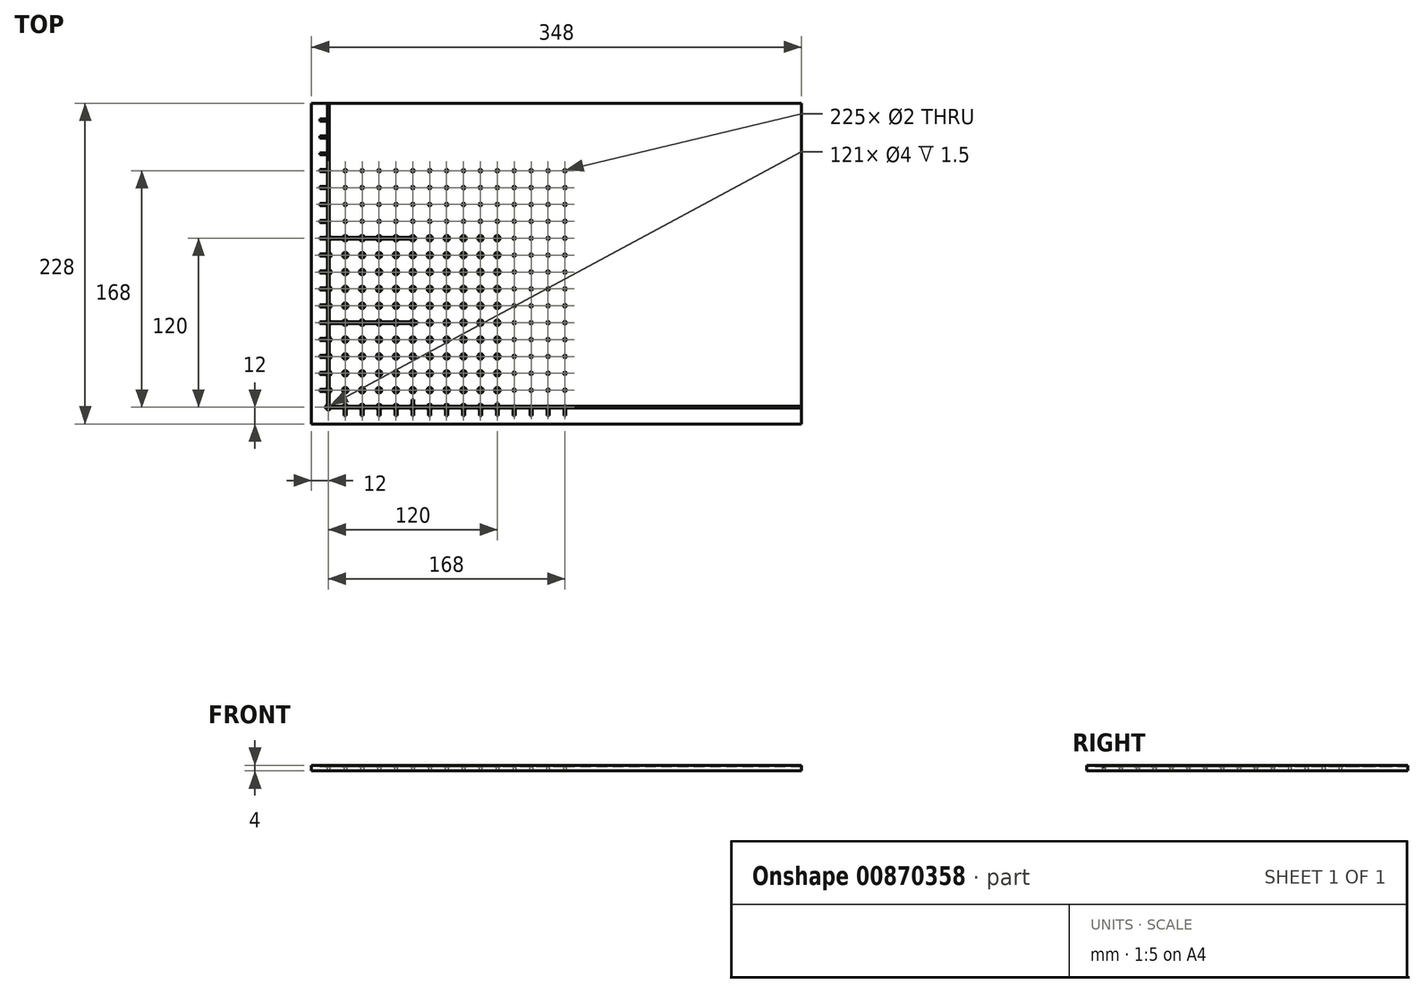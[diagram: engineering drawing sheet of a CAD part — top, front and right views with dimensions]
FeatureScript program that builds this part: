
annotation { "Feature Type Name" : "Feature", "Feature Type Description" : "" }
export const myFeature = defineFeature(function(context is Context, id is Id, definition is map)
    precondition{}
    {
        {
            var Q0;
            Q0=qCreatedBy(makeId("Top.planeOp"),FACE);
            var sketch = newSketch(context, id + "F0", { "sketchPlane" : qUnion([Q0])});
            skLineSegment(sketch, "E0.bottom", {"start": v(-174, -114) * mm, "end": v(174, -114) * mm});
            skLineSegment(sketch, "E0.top", {"start": v(-174, 114) * mm, "end": v(174, 114) * mm});
            skLineSegment(sketch, "E0.left", {"start": v(-174, -114) * mm, "end": v(-174, 114) * mm});
            skLineSegment(sketch, "E0.right", {"start": v(174, -114) * mm, "end": v(174, 114) * mm});
            skPoint(sketch, "E0.middle", {"position": v(-82, -38) * mm});
            skCircle(sketch, "E1", {"center": v(-162, 66) * mm, "radius": 1 * mm});
            skCircle(sketch, "E2.0.1.0", {"center": v(-162, 54) * mm, "radius": 1 * mm});
            skCircle(sketch, "E2.0.2.0", {"center": v(-162, 42) * mm, "radius": 1 * mm});
            skCircle(sketch, "E2.0.3.0", {"center": v(-162, 30) * mm, "radius": 1 * mm});
            skCircle(sketch, "E2.0.4.0", {"center": v(-162, 18) * mm, "radius": 1 * mm});
            skCircle(sketch, "E2.0.5.0", {"center": v(-162, 6) * mm, "radius": 1 * mm});
            skCircle(sketch, "E2.0.6.0", {"center": v(-162, -6) * mm, "radius": 1 * mm});
            skCircle(sketch, "E2.0.7.0", {"center": v(-162, -18) * mm, "radius": 1 * mm});
            skCircle(sketch, "E2.0.8.0", {"center": v(-162, -30) * mm, "radius": 1 * mm});
            skCircle(sketch, "E2.0.9.0", {"center": v(-162, -42) * mm, "radius": 1 * mm});
            skCircle(sketch, "E2.0.10.0", {"center": v(-162, -54) * mm, "radius": 1 * mm});
            skCircle(sketch, "E2.0.11.0", {"center": v(-162, -66) * mm, "radius": 1 * mm});
            skCircle(sketch, "E2.0.12.0", {"center": v(-162, -78) * mm, "radius": 1 * mm});
            skCircle(sketch, "E2.0.13.0", {"center": v(-162, -90) * mm, "radius": 1 * mm});
            skCircle(sketch, "E2.0.14.0", {"center": v(-162, -102) * mm, "radius": 1 * mm});
            skLineSegment(sketch, "E2.direction1", {"start": v(-162, 66) * mm, "end": v(-150, 66) * mm, "construction": true});
            skLineSegment(sketch, "E2.direction2", {"start": v(-162, 66) * mm, "end": v(-162, 54) * mm, "construction": true});
            skCircle(sketch, "E3.0.1.0", {"center": v(-150, 66) * mm, "radius": 1 * mm});
            skCircle(sketch, "E3.0.1.1", {"center": v(-150, 54) * mm, "radius": 1 * mm});
            skCircle(sketch, "E3.0.1.2", {"center": v(-150, 42) * mm, "radius": 1 * mm});
            skCircle(sketch, "E3.0.1.3", {"center": v(-150, 30) * mm, "radius": 1 * mm});
            skCircle(sketch, "E3.0.1.4", {"center": v(-150, 18) * mm, "radius": 1 * mm});
            skCircle(sketch, "E3.0.1.5", {"center": v(-150, 6) * mm, "radius": 1 * mm});
            skCircle(sketch, "E3.0.1.6", {"center": v(-150, -6) * mm, "radius": 1 * mm});
            skCircle(sketch, "E3.0.1.7", {"center": v(-150, -18) * mm, "radius": 1 * mm});
            skCircle(sketch, "E3.0.1.8", {"center": v(-150, -30) * mm, "radius": 1 * mm});
            skCircle(sketch, "E3.0.1.9", {"center": v(-150, -42) * mm, "radius": 1 * mm});
            skCircle(sketch, "E3.0.1.10", {"center": v(-150, -54) * mm, "radius": 1 * mm});
            skCircle(sketch, "E3.0.1.11", {"center": v(-150, -66) * mm, "radius": 1 * mm});
            skCircle(sketch, "E3.0.1.12", {"center": v(-150, -78) * mm, "radius": 1 * mm});
            skCircle(sketch, "E3.0.1.13", {"center": v(-150, -90) * mm, "radius": 1 * mm});
            skCircle(sketch, "E3.0.1.14", {"center": v(-150, -102) * mm, "radius": 1 * mm});
            skCircle(sketch, "E3.0.2.0", {"center": v(-138, 66) * mm, "radius": 1 * mm});
            skCircle(sketch, "E3.0.2.1", {"center": v(-138, 54) * mm, "radius": 1 * mm});
            skCircle(sketch, "E3.0.2.2", {"center": v(-138, 42) * mm, "radius": 1 * mm});
            skCircle(sketch, "E3.0.2.3", {"center": v(-138, 30) * mm, "radius": 1 * mm});
            skCircle(sketch, "E3.0.2.4", {"center": v(-138, 18) * mm, "radius": 1 * mm});
            skCircle(sketch, "E3.0.2.5", {"center": v(-138, 6) * mm, "radius": 1 * mm});
            skCircle(sketch, "E3.0.2.6", {"center": v(-138, -6) * mm, "radius": 1 * mm});
            skCircle(sketch, "E3.0.2.7", {"center": v(-138, -18) * mm, "radius": 1 * mm});
            skCircle(sketch, "E3.0.2.8", {"center": v(-138, -30) * mm, "radius": 1 * mm});
            skCircle(sketch, "E3.0.2.9", {"center": v(-138, -42) * mm, "radius": 1 * mm});
            skCircle(sketch, "E3.0.2.10", {"center": v(-138, -54) * mm, "radius": 1 * mm});
            skCircle(sketch, "E3.0.2.11", {"center": v(-138, -66) * mm, "radius": 1 * mm});
            skCircle(sketch, "E3.0.2.12", {"center": v(-138, -78) * mm, "radius": 1 * mm});
            skCircle(sketch, "E3.0.2.13", {"center": v(-138, -90) * mm, "radius": 1 * mm});
            skCircle(sketch, "E3.0.2.14", {"center": v(-138, -102) * mm, "radius": 1 * mm});
            skCircle(sketch, "E3.0.3.0", {"center": v(-126, 66) * mm, "radius": 1 * mm});
            skCircle(sketch, "E3.0.3.1", {"center": v(-126, 54) * mm, "radius": 1 * mm});
            skCircle(sketch, "E3.0.3.2", {"center": v(-126, 42) * mm, "radius": 1 * mm});
            skCircle(sketch, "E3.0.3.3", {"center": v(-126, 30) * mm, "radius": 1 * mm});
            skCircle(sketch, "E3.0.3.4", {"center": v(-126, 18) * mm, "radius": 1 * mm});
            skCircle(sketch, "E3.0.3.5", {"center": v(-126, 6) * mm, "radius": 1 * mm});
            skCircle(sketch, "E3.0.3.6", {"center": v(-126, -6) * mm, "radius": 1 * mm});
            skCircle(sketch, "E3.0.3.7", {"center": v(-126, -18) * mm, "radius": 1 * mm});
            skCircle(sketch, "E3.0.3.8", {"center": v(-126, -30) * mm, "radius": 1 * mm});
            skCircle(sketch, "E3.0.3.9", {"center": v(-126, -42) * mm, "radius": 1 * mm});
            skCircle(sketch, "E3.0.3.10", {"center": v(-126, -54) * mm, "radius": 1 * mm});
            skCircle(sketch, "E3.0.3.11", {"center": v(-126, -66) * mm, "radius": 1 * mm});
            skCircle(sketch, "E3.0.3.12", {"center": v(-126, -78) * mm, "radius": 1 * mm});
            skCircle(sketch, "E3.0.3.13", {"center": v(-126, -90) * mm, "radius": 1 * mm});
            skCircle(sketch, "E3.0.3.14", {"center": v(-126, -102) * mm, "radius": 1 * mm});
            skCircle(sketch, "E3.0.4.0", {"center": v(-114, 66) * mm, "radius": 1 * mm});
            skCircle(sketch, "E3.0.4.1", {"center": v(-114, 54) * mm, "radius": 1 * mm});
            skCircle(sketch, "E3.0.4.2", {"center": v(-114, 42) * mm, "radius": 1 * mm});
            skCircle(sketch, "E3.0.4.3", {"center": v(-114, 30) * mm, "radius": 1 * mm});
            skCircle(sketch, "E3.0.4.4", {"center": v(-114, 18) * mm, "radius": 1 * mm});
            skCircle(sketch, "E3.0.4.5", {"center": v(-114, 6) * mm, "radius": 1 * mm});
            skCircle(sketch, "E3.0.4.6", {"center": v(-114, -6) * mm, "radius": 1 * mm});
            skCircle(sketch, "E3.0.4.7", {"center": v(-114, -18) * mm, "radius": 1 * mm});
            skCircle(sketch, "E3.0.4.8", {"center": v(-114, -30) * mm, "radius": 1 * mm});
            skCircle(sketch, "E3.0.4.9", {"center": v(-114, -42) * mm, "radius": 1 * mm});
            skCircle(sketch, "E3.0.4.10", {"center": v(-114, -54) * mm, "radius": 1 * mm});
            skCircle(sketch, "E3.0.4.11", {"center": v(-114, -66) * mm, "radius": 1 * mm});
            skCircle(sketch, "E3.0.4.12", {"center": v(-114, -78) * mm, "radius": 1 * mm});
            skCircle(sketch, "E3.0.4.13", {"center": v(-114, -90) * mm, "radius": 1 * mm});
            skCircle(sketch, "E3.0.4.14", {"center": v(-114, -102) * mm, "radius": 1 * mm});
            skCircle(sketch, "E3.0.5.0", {"center": v(-102, 66) * mm, "radius": 1 * mm});
            skCircle(sketch, "E3.0.5.1", {"center": v(-102, 54) * mm, "radius": 1 * mm});
            skCircle(sketch, "E3.0.5.2", {"center": v(-102, 42) * mm, "radius": 1 * mm});
            skCircle(sketch, "E3.0.5.3", {"center": v(-102, 30) * mm, "radius": 1 * mm});
            skCircle(sketch, "E3.0.5.4", {"center": v(-102, 18) * mm, "radius": 1 * mm});
            skCircle(sketch, "E3.0.5.5", {"center": v(-102, 6) * mm, "radius": 1 * mm});
            skCircle(sketch, "E3.0.5.6", {"center": v(-102, -6) * mm, "radius": 1 * mm});
            skCircle(sketch, "E3.0.5.7", {"center": v(-102, -18) * mm, "radius": 1 * mm});
            skCircle(sketch, "E3.0.5.8", {"center": v(-102, -30) * mm, "radius": 1 * mm});
            skCircle(sketch, "E3.0.5.9", {"center": v(-102, -42) * mm, "radius": 1 * mm});
            skCircle(sketch, "E3.0.5.10", {"center": v(-102, -54) * mm, "radius": 1 * mm});
            skCircle(sketch, "E3.0.5.11", {"center": v(-102, -66) * mm, "radius": 1 * mm});
            skCircle(sketch, "E3.0.5.12", {"center": v(-102, -78) * mm, "radius": 1 * mm});
            skCircle(sketch, "E3.0.5.13", {"center": v(-102, -90) * mm, "radius": 1 * mm});
            skCircle(sketch, "E3.0.5.14", {"center": v(-102, -102) * mm, "radius": 1 * mm});
            skCircle(sketch, "E3.0.6.0", {"center": v(-90, 66) * mm, "radius": 1 * mm});
            skCircle(sketch, "E3.0.6.1", {"center": v(-90, 54) * mm, "radius": 1 * mm});
            skCircle(sketch, "E3.0.6.2", {"center": v(-90, 42) * mm, "radius": 1 * mm});
            skCircle(sketch, "E3.0.6.3", {"center": v(-90, 30) * mm, "radius": 1 * mm});
            skCircle(sketch, "E3.0.6.4", {"center": v(-90, 18) * mm, "radius": 1 * mm});
            skCircle(sketch, "E3.0.6.5", {"center": v(-90, 6) * mm, "radius": 1 * mm});
            skCircle(sketch, "E3.0.6.6", {"center": v(-90, -6) * mm, "radius": 1 * mm});
            skCircle(sketch, "E3.0.6.7", {"center": v(-90, -18) * mm, "radius": 1 * mm});
            skCircle(sketch, "E3.0.6.8", {"center": v(-90, -30) * mm, "radius": 1 * mm});
            skCircle(sketch, "E3.0.6.9", {"center": v(-90, -42) * mm, "radius": 1 * mm});
            skCircle(sketch, "E3.0.6.10", {"center": v(-90, -54) * mm, "radius": 1 * mm});
            skCircle(sketch, "E3.0.6.11", {"center": v(-90, -66) * mm, "radius": 1 * mm});
            skCircle(sketch, "E3.0.6.12", {"center": v(-90, -78) * mm, "radius": 1 * mm});
            skCircle(sketch, "E3.0.6.13", {"center": v(-90, -90) * mm, "radius": 1 * mm});
            skCircle(sketch, "E3.0.6.14", {"center": v(-90, -102) * mm, "radius": 1 * mm});
            skCircle(sketch, "E3.0.7.0", {"center": v(-78, 66) * mm, "radius": 1 * mm});
            skCircle(sketch, "E3.0.7.1", {"center": v(-78, 54) * mm, "radius": 1 * mm});
            skCircle(sketch, "E3.0.7.2", {"center": v(-78, 42) * mm, "radius": 1 * mm});
            skCircle(sketch, "E3.0.7.3", {"center": v(-78, 30) * mm, "radius": 1 * mm});
            skCircle(sketch, "E3.0.7.4", {"center": v(-78, 18) * mm, "radius": 1 * mm});
            skCircle(sketch, "E3.0.7.5", {"center": v(-78, 6) * mm, "radius": 1 * mm});
            skCircle(sketch, "E3.0.7.6", {"center": v(-78, -6) * mm, "radius": 1 * mm});
            skCircle(sketch, "E3.0.7.7", {"center": v(-78, -18) * mm, "radius": 1 * mm});
            skCircle(sketch, "E3.0.7.8", {"center": v(-78, -30) * mm, "radius": 1 * mm});
            skCircle(sketch, "E3.0.7.9", {"center": v(-78, -42) * mm, "radius": 1 * mm});
            skCircle(sketch, "E3.0.7.10", {"center": v(-78, -54) * mm, "radius": 1 * mm});
            skCircle(sketch, "E3.0.7.11", {"center": v(-78, -66) * mm, "radius": 1 * mm});
            skCircle(sketch, "E3.0.7.12", {"center": v(-78, -78) * mm, "radius": 1 * mm});
            skCircle(sketch, "E3.0.7.13", {"center": v(-78, -90) * mm, "radius": 1 * mm});
            skCircle(sketch, "E3.0.7.14", {"center": v(-78, -102) * mm, "radius": 1 * mm});
            skCircle(sketch, "E3.0.8.0", {"center": v(-66, 66) * mm, "radius": 1 * mm});
            skCircle(sketch, "E3.0.8.1", {"center": v(-66, 54) * mm, "radius": 1 * mm});
            skCircle(sketch, "E3.0.8.2", {"center": v(-66, 42) * mm, "radius": 1 * mm});
            skCircle(sketch, "E3.0.8.3", {"center": v(-66, 30) * mm, "radius": 1 * mm});
            skCircle(sketch, "E3.0.8.4", {"center": v(-66, 18) * mm, "radius": 1 * mm});
            skCircle(sketch, "E3.0.8.5", {"center": v(-66, 6) * mm, "radius": 1 * mm});
            skCircle(sketch, "E3.0.8.6", {"center": v(-66, -6) * mm, "radius": 1 * mm});
            skCircle(sketch, "E3.0.8.7", {"center": v(-66, -18) * mm, "radius": 1 * mm});
            skCircle(sketch, "E3.0.8.8", {"center": v(-66, -30) * mm, "radius": 1 * mm});
            skCircle(sketch, "E3.0.8.9", {"center": v(-66, -42) * mm, "radius": 1 * mm});
            skCircle(sketch, "E3.0.8.10", {"center": v(-66, -54) * mm, "radius": 1 * mm});
            skCircle(sketch, "E3.0.8.11", {"center": v(-66, -66) * mm, "radius": 1 * mm});
            skCircle(sketch, "E3.0.8.12", {"center": v(-66, -78) * mm, "radius": 1 * mm});
            skCircle(sketch, "E3.0.8.13", {"center": v(-66, -90) * mm, "radius": 1 * mm});
            skCircle(sketch, "E3.0.8.14", {"center": v(-66, -102) * mm, "radius": 1 * mm});
            skCircle(sketch, "E3.0.9.0", {"center": v(-54, 66) * mm, "radius": 1 * mm});
            skCircle(sketch, "E3.0.9.1", {"center": v(-54, 54) * mm, "radius": 1 * mm});
            skCircle(sketch, "E3.0.9.2", {"center": v(-54, 42) * mm, "radius": 1 * mm});
            skCircle(sketch, "E3.0.9.3", {"center": v(-54, 30) * mm, "radius": 1 * mm});
            skCircle(sketch, "E3.0.9.4", {"center": v(-54, 18) * mm, "radius": 1 * mm});
            skCircle(sketch, "E3.0.9.5", {"center": v(-54, 6) * mm, "radius": 1 * mm});
            skCircle(sketch, "E3.0.9.6", {"center": v(-54, -6) * mm, "radius": 1 * mm});
            skCircle(sketch, "E3.0.9.7", {"center": v(-54, -18) * mm, "radius": 1 * mm});
            skCircle(sketch, "E3.0.9.8", {"center": v(-54, -30) * mm, "radius": 1 * mm});
            skCircle(sketch, "E3.0.9.9", {"center": v(-54, -42) * mm, "radius": 1 * mm});
            skCircle(sketch, "E3.0.9.10", {"center": v(-54, -54) * mm, "radius": 1 * mm});
            skCircle(sketch, "E3.0.9.11", {"center": v(-54, -66) * mm, "radius": 1 * mm});
            skCircle(sketch, "E3.0.9.12", {"center": v(-54, -78) * mm, "radius": 1 * mm});
            skCircle(sketch, "E3.0.9.13", {"center": v(-54, -90) * mm, "radius": 1 * mm});
            skCircle(sketch, "E3.0.9.14", {"center": v(-54, -102) * mm, "radius": 1 * mm});
            skCircle(sketch, "E3.0.10.0", {"center": v(-42, 66) * mm, "radius": 1 * mm});
            skCircle(sketch, "E3.0.10.1", {"center": v(-42, 54) * mm, "radius": 1 * mm});
            skCircle(sketch, "E3.0.10.2", {"center": v(-42, 42) * mm, "radius": 1 * mm});
            skCircle(sketch, "E3.0.10.3", {"center": v(-42, 30) * mm, "radius": 1 * mm});
            skCircle(sketch, "E3.0.10.4", {"center": v(-42, 18) * mm, "radius": 1 * mm});
            skCircle(sketch, "E3.0.10.5", {"center": v(-42, 6) * mm, "radius": 1 * mm});
            skCircle(sketch, "E3.0.10.6", {"center": v(-42, -6) * mm, "radius": 1 * mm});
            skCircle(sketch, "E3.0.10.7", {"center": v(-42, -18) * mm, "radius": 1 * mm});
            skCircle(sketch, "E3.0.10.8", {"center": v(-42, -30) * mm, "radius": 1 * mm});
            skCircle(sketch, "E3.0.10.9", {"center": v(-42, -42) * mm, "radius": 1 * mm});
            skCircle(sketch, "E3.0.10.10", {"center": v(-42, -54) * mm, "radius": 1 * mm});
            skCircle(sketch, "E3.0.10.11", {"center": v(-42, -66) * mm, "radius": 1 * mm});
            skCircle(sketch, "E3.0.10.12", {"center": v(-42, -78) * mm, "radius": 1 * mm});
            skCircle(sketch, "E3.0.10.13", {"center": v(-42, -90) * mm, "radius": 1 * mm});
            skCircle(sketch, "E3.0.10.14", {"center": v(-42, -102) * mm, "radius": 1 * mm});
            skCircle(sketch, "E3.0.11.0", {"center": v(-30, 66) * mm, "radius": 1 * mm});
            skCircle(sketch, "E3.0.11.1", {"center": v(-30, 54) * mm, "radius": 1 * mm});
            skCircle(sketch, "E3.0.11.2", {"center": v(-30, 42) * mm, "radius": 1 * mm});
            skCircle(sketch, "E3.0.11.3", {"center": v(-30, 30) * mm, "radius": 1 * mm});
            skCircle(sketch, "E3.0.11.4", {"center": v(-30, 18) * mm, "radius": 1 * mm});
            skCircle(sketch, "E3.0.11.5", {"center": v(-30, 6) * mm, "radius": 1 * mm});
            skCircle(sketch, "E3.0.11.6", {"center": v(-30, -6) * mm, "radius": 1 * mm});
            skCircle(sketch, "E3.0.11.7", {"center": v(-30, -18) * mm, "radius": 1 * mm});
            skCircle(sketch, "E3.0.11.8", {"center": v(-30, -30) * mm, "radius": 1 * mm});
            skCircle(sketch, "E3.0.11.9", {"center": v(-30, -42) * mm, "radius": 1 * mm});
            skCircle(sketch, "E3.0.11.10", {"center": v(-30, -54) * mm, "radius": 1 * mm});
            skCircle(sketch, "E3.0.11.11", {"center": v(-30, -66) * mm, "radius": 1 * mm});
            skCircle(sketch, "E3.0.11.12", {"center": v(-30, -78) * mm, "radius": 1 * mm});
            skCircle(sketch, "E3.0.11.13", {"center": v(-30, -90) * mm, "radius": 1 * mm});
            skCircle(sketch, "E3.0.11.14", {"center": v(-30, -102) * mm, "radius": 1 * mm});
            skCircle(sketch, "E3.0.12.0", {"center": v(-18, 66) * mm, "radius": 1 * mm});
            skCircle(sketch, "E3.0.12.1", {"center": v(-18, 54) * mm, "radius": 1 * mm});
            skCircle(sketch, "E3.0.12.2", {"center": v(-18, 42) * mm, "radius": 1 * mm});
            skCircle(sketch, "E3.0.12.3", {"center": v(-18, 30) * mm, "radius": 1 * mm});
            skCircle(sketch, "E3.0.12.4", {"center": v(-18, 18) * mm, "radius": 1 * mm});
            skCircle(sketch, "E3.0.12.5", {"center": v(-18, 6) * mm, "radius": 1 * mm});
            skCircle(sketch, "E3.0.12.6", {"center": v(-18, -6) * mm, "radius": 1 * mm});
            skCircle(sketch, "E3.0.12.7", {"center": v(-18, -18) * mm, "radius": 1 * mm});
            skCircle(sketch, "E3.0.12.8", {"center": v(-18, -30) * mm, "radius": 1 * mm});
            skCircle(sketch, "E3.0.12.9", {"center": v(-18, -42) * mm, "radius": 1 * mm});
            skCircle(sketch, "E3.0.12.10", {"center": v(-18, -54) * mm, "radius": 1 * mm});
            skCircle(sketch, "E3.0.12.11", {"center": v(-18, -66) * mm, "radius": 1 * mm});
            skCircle(sketch, "E3.0.12.12", {"center": v(-18, -78) * mm, "radius": 1 * mm});
            skCircle(sketch, "E3.0.12.13", {"center": v(-18, -90) * mm, "radius": 1 * mm});
            skCircle(sketch, "E3.0.12.14", {"center": v(-18, -102) * mm, "radius": 1 * mm});
            skCircle(sketch, "E3.0.13.0", {"center": v(-6, 66) * mm, "radius": 1 * mm});
            skCircle(sketch, "E3.0.13.1", {"center": v(-6, 54) * mm, "radius": 1 * mm});
            skCircle(sketch, "E3.0.13.2", {"center": v(-6, 42) * mm, "radius": 1 * mm});
            skCircle(sketch, "E3.0.13.3", {"center": v(-6, 30) * mm, "radius": 1 * mm});
            skCircle(sketch, "E3.0.13.4", {"center": v(-6, 18) * mm, "radius": 1 * mm});
            skCircle(sketch, "E3.0.13.5", {"center": v(-6, 6) * mm, "radius": 1 * mm});
            skCircle(sketch, "E3.0.13.6", {"center": v(-6, -6) * mm, "radius": 1 * mm});
            skCircle(sketch, "E3.0.13.7", {"center": v(-6, -18) * mm, "radius": 1 * mm});
            skCircle(sketch, "E3.0.13.8", {"center": v(-6, -30) * mm, "radius": 1 * mm});
            skCircle(sketch, "E3.0.13.9", {"center": v(-6, -42) * mm, "radius": 1 * mm});
            skCircle(sketch, "E3.0.13.10", {"center": v(-6, -54) * mm, "radius": 1 * mm});
            skCircle(sketch, "E3.0.13.11", {"center": v(-6, -66) * mm, "radius": 1 * mm});
            skCircle(sketch, "E3.0.13.12", {"center": v(-6, -78) * mm, "radius": 1 * mm});
            skCircle(sketch, "E3.0.13.13", {"center": v(-6, -90) * mm, "radius": 1 * mm});
            skCircle(sketch, "E3.0.13.14", {"center": v(-6, -102) * mm, "radius": 1 * mm});
            skCircle(sketch, "E3.0.14.0", {"center": v(6, 66) * mm, "radius": 1 * mm});
            skCircle(sketch, "E3.0.14.1", {"center": v(6, 54) * mm, "radius": 1 * mm});
            skCircle(sketch, "E3.0.14.2", {"center": v(6, 42) * mm, "radius": 1 * mm});
            skCircle(sketch, "E3.0.14.3", {"center": v(6, 30) * mm, "radius": 1 * mm});
            skCircle(sketch, "E3.0.14.4", {"center": v(6, 18) * mm, "radius": 1 * mm});
            skCircle(sketch, "E3.0.14.5", {"center": v(6, 6) * mm, "radius": 1 * mm});
            skCircle(sketch, "E3.0.14.6", {"center": v(6, -6) * mm, "radius": 1 * mm});
            skCircle(sketch, "E3.0.14.7", {"center": v(6, -18) * mm, "radius": 1 * mm});
            skCircle(sketch, "E3.0.14.8", {"center": v(6, -30) * mm, "radius": 1 * mm});
            skCircle(sketch, "E3.0.14.9", {"center": v(6, -42) * mm, "radius": 1 * mm});
            skCircle(sketch, "E3.0.14.10", {"center": v(6, -54) * mm, "radius": 1 * mm});
            skCircle(sketch, "E3.0.14.11", {"center": v(6, -66) * mm, "radius": 1 * mm});
            skCircle(sketch, "E3.0.14.12", {"center": v(6, -78) * mm, "radius": 1 * mm});
            skCircle(sketch, "E3.0.14.13", {"center": v(6, -90) * mm, "radius": 1 * mm});
            skCircle(sketch, "E3.0.14.14", {"center": v(6, -102) * mm, "radius": 1 * mm});
            skLineSegment(sketch, "E4", {"start": v(-187.06, -102) * mm, "end": v(211.47, -102) * mm, "construction": true});
            skLineSegment(sketch, "E5", {"start": v(-162, 132.06) * mm, "end": v(-162, -148.74) * mm, "construction": true});
            skSolve(sketch);
        }
        {
            var Q0;
            Q0=qSketchRegion(id+"F0",true);
            extrude(context, id + "F1", {"entities" : qUnion([Q0]), "offsetDistance" : 25 * mm, "depth" : 4 * mm});
        }
        {
            var Q0;
            Q0=makeQuery(id+"F1.opExtrude","CAP_FACE",FACE,{"disambiguationData":[OSD([sQuery(id+"F0.wireOp",EDGE,"E0.bottom"),sQuery(id+"F0.wireOp",EDGE,"E0.top"),sQuery(id+"F0.wireOp",EDGE,"E0.left"),sQuery(id+"F0.wireOp",EDGE,"E0.right"),sQuery(id+"F0.wireOp",EDGE,"E1"),sQuery(id+"F0.wireOp",EDGE,"E2.0.1.0"),sQuery(id+"F0.wireOp",EDGE,"E2.0.2.0"),sQuery(id+"F0.wireOp",EDGE,"E2.0.3.0"),sQuery(id+"F0.wireOp",EDGE,"E2.0.4.0"),sQuery(id+"F0.wireOp",EDGE,"E2.0.5.0"),sQuery(id+"F0.wireOp",EDGE,"E2.0.6.0"),sQuery(id+"F0.wireOp",EDGE,"E2.0.7.0"),sQuery(id+"F0.wireOp",EDGE,"E2.0.8.0"),sQuery(id+"F0.wireOp",EDGE,"E2.0.9.0"),sQuery(id+"F0.wireOp",EDGE,"E2.0.10.0"),sQuery(id+"F0.wireOp",EDGE,"E2.0.11.0"),sQuery(id+"F0.wireOp",EDGE,"E2.0.12.0"),sQuery(id+"F0.wireOp",EDGE,"E2.0.13.0"),sQuery(id+"F0.wireOp",EDGE,"E2.0.14.0"),sQuery(id+"F0.wireOp",EDGE,"E2.0.15.0"),sQuery(id+"F0.wireOp",EDGE,"E2.1.0.0"),sQuery(id+"F0.wireOp",EDGE,"E2.1.1.0"),sQuery(id+"F0.wireOp",EDGE,"E2.1.2.0"),sQuery(id+"F0.wireOp",EDGE,"E2.1.3.0"),sQuery(id+"F0.wireOp",EDGE,"E2.1.4.0"),sQuery(id+"F0.wireOp",EDGE,"E2.1.5.0"),sQuery(id+"F0.wireOp",EDGE,"E2.1.6.0"),sQuery(id+"F0.wireOp",EDGE,"E2.1.7.0"),sQuery(id+"F0.wireOp",EDGE,"E2.1.8.0"),sQuery(id+"F0.wireOp",EDGE,"E2.1.9.0"),sQuery(id+"F0.wireOp",EDGE,"E2.1.10.0"),sQuery(id+"F0.wireOp",EDGE,"E2.1.11.0"),sQuery(id+"F0.wireOp",EDGE,"E2.1.12.0"),sQuery(id+"F0.wireOp",EDGE,"E2.1.13.0"),sQuery(id+"F0.wireOp",EDGE,"E2.1.14.0"),sQuery(id+"F0.wireOp",EDGE,"E2.1.15.0"),sQuery(id+"F0.wireOp",EDGE,"E2.2.0.0"),sQuery(id+"F0.wireOp",EDGE,"E2.2.1.0"),sQuery(id+"F0.wireOp",EDGE,"E2.2.2.0"),sQuery(id+"F0.wireOp",EDGE,"E2.2.3.0"),sQuery(id+"F0.wireOp",EDGE,"E2.2.4.0"),sQuery(id+"F0.wireOp",EDGE,"E2.2.5.0"),sQuery(id+"F0.wireOp",EDGE,"E2.2.6.0"),sQuery(id+"F0.wireOp",EDGE,"E2.2.7.0"),sQuery(id+"F0.wireOp",EDGE,"E2.2.8.0"),sQuery(id+"F0.wireOp",EDGE,"E2.2.9.0"),sQuery(id+"F0.wireOp",EDGE,"E2.2.10.0"),sQuery(id+"F0.wireOp",EDGE,"E2.2.11.0"),sQuery(id+"F0.wireOp",EDGE,"E2.2.12.0"),sQuery(id+"F0.wireOp",EDGE,"E2.2.13.0"),sQuery(id+"F0.wireOp",EDGE,"E2.2.14.0"),sQuery(id+"F0.wireOp",EDGE,"E2.2.15.0"),sQuery(id+"F0.wireOp",EDGE,"E2.3.0.0"),sQuery(id+"F0.wireOp",EDGE,"E2.3.1.0"),sQuery(id+"F0.wireOp",EDGE,"E2.3.11.0"),sQuery(id+"F0.wireOp",EDGE,"E2.3.12.0"),sQuery(id+"F0.wireOp",EDGE,"E2.3.13.0"),sQuery(id+"F0.wireOp",EDGE,"E2.3.14.0"),sQuery(id+"F0.wireOp",EDGE,"E2.3.15.0"),sQuery(id+"F0.wireOp",EDGE,"E2.4.0.0"),sQuery(id+"F0.wireOp",EDGE,"E2.4.1.0"),sQuery(id+"F0.wireOp",EDGE,"E2.4.2.0"),sQuery(id+"F0.wireOp",EDGE,"E2.4.11.0"),sQuery(id+"F0.wireOp",EDGE,"E2.4.12.0"),sQuery(id+"F0.wireOp",EDGE,"E2.4.13.0"),sQuery(id+"F0.wireOp",EDGE,"E2.4.14.0"),sQuery(id+"F0.wireOp",EDGE,"E2.4.15.0"),sQuery(id+"F0.wireOp",EDGE,"E2.5.0.0"),sQuery(id+"F0.wireOp",EDGE,"E2.5.1.0"),sQuery(id+"F0.wireOp",EDGE,"E2.5.11.0"),sQuery(id+"F0.wireOp",EDGE,"E2.5.12.0"),sQuery(id+"F0.wireOp",EDGE,"E2.5.13.0"),sQuery(id+"F0.wireOp",EDGE,"E2.5.14.0"),sQuery(id+"F0.wireOp",EDGE,"E2.5.15.0"),sQuery(id+"F0.wireOp",EDGE,"E2.6.0.0"),sQuery(id+"F0.wireOp",EDGE,"E2.6.1.0"),sQuery(id+"F0.wireOp",EDGE,"E2.6.2.0"),sQuery(id+"F0.wireOp",EDGE,"E2.6.11.0"),sQuery(id+"F0.wireOp",EDGE,"E2.6.12.0"),sQuery(id+"F0.wireOp",EDGE,"E2.6.13.0"),sQuery(id+"F0.wireOp",EDGE,"E2.6.14.0"),sQuery(id+"F0.wireOp",EDGE,"E2.6.15.0"),sQuery(id+"F0.wireOp",EDGE,"E2.7.0.0"),sQuery(id+"F0.wireOp",EDGE,"E2.7.1.0"),sQuery(id+"F0.wireOp",EDGE,"E2.7.2.0"),sQuery(id+"F0.wireOp",EDGE,"E2.7.3.0"),sQuery(id+"F0.wireOp",EDGE,"E2.7.4.0"),sQuery(id+"F0.wireOp",EDGE,"E2.7.5.0"),sQuery(id+"F0.wireOp",EDGE,"E2.7.6.0"),sQuery(id+"F0.wireOp",EDGE,"E2.7.7.0"),sQuery(id+"F0.wireOp",EDGE,"E2.7.8.0"),sQuery(id+"F0.wireOp",EDGE,"E2.7.9.0"),sQuery(id+"F0.wireOp",EDGE,"E2.7.10.0"),sQuery(id+"F0.wireOp",EDGE,"E2.7.11.0"),sQuery(id+"F0.wireOp",EDGE,"E2.7.12.0"),sQuery(id+"F0.wireOp",EDGE,"E2.7.13.0"),sQuery(id+"F0.wireOp",EDGE,"E2.7.14.0"),sQuery(id+"F0.wireOp",EDGE,"E2.7.15.0"),sQuery(id+"F0.wireOp",EDGE,"E2.8.0.0"),sQuery(id+"F0.wireOp",EDGE,"E2.8.1.0"),sQuery(id+"F0.wireOp",EDGE,"E2.8.2.0"),sQuery(id+"F0.wireOp",EDGE,"E2.8.3.0"),sQuery(id+"F0.wireOp",EDGE,"E2.8.4.0"),sQuery(id+"F0.wireOp",EDGE,"E2.8.5.0"),sQuery(id+"F0.wireOp",EDGE,"E2.8.6.0"),sQuery(id+"F0.wireOp",EDGE,"E2.8.7.0"),sQuery(id+"F0.wireOp",EDGE,"E2.8.8.0"),sQuery(id+"F0.wireOp",EDGE,"E2.8.9.0"),sQuery(id+"F0.wireOp",EDGE,"E2.8.10.0"),sQuery(id+"F0.wireOp",EDGE,"E2.8.11.0"),sQuery(id+"F0.wireOp",EDGE,"E2.8.12.0"),sQuery(id+"F0.wireOp",EDGE,"E2.8.13.0"),sQuery(id+"F0.wireOp",EDGE,"E2.8.14.0"),sQuery(id+"F0.wireOp",EDGE,"E2.8.15.0"),sQuery(id+"F0.wireOp",EDGE,"E2.9.0.0"),sQuery(id+"F0.wireOp",EDGE,"E2.9.1.0"),sQuery(id+"F0.wireOp",EDGE,"E2.9.2.0"),sQuery(id+"F0.wireOp",EDGE,"E2.9.3.0"),sQuery(id+"F0.wireOp",EDGE,"E2.9.4.0"),sQuery(id+"F0.wireOp",EDGE,"E2.9.5.0"),sQuery(id+"F0.wireOp",EDGE,"E2.9.6.0"),sQuery(id+"F0.wireOp",EDGE,"E2.9.7.0"),sQuery(id+"F0.wireOp",EDGE,"E2.9.8.0"),sQuery(id+"F0.wireOp",EDGE,"E2.9.9.0"),sQuery(id+"F0.wireOp",EDGE,"E2.9.10.0"),sQuery(id+"F0.wireOp",EDGE,"E2.9.11.0"),sQuery(id+"F0.wireOp",EDGE,"E2.9.12.0"),sQuery(id+"F0.wireOp",EDGE,"E2.9.13.0"),sQuery(id+"F0.wireOp",EDGE,"E2.9.14.0"),sQuery(id+"F0.wireOp",EDGE,"E2.9.15.0"),sQuery(id+"F0.wireOp",EDGE,"E2.10.0.0"),sQuery(id+"F0.wireOp",EDGE,"E2.10.1.0"),sQuery(id+"F0.wireOp",EDGE,"E2.10.2.0"),sQuery(id+"F0.wireOp",EDGE,"E2.10.3.0"),sQuery(id+"F0.wireOp",EDGE,"E2.10.4.0"),sQuery(id+"F0.wireOp",EDGE,"E2.10.5.0"),sQuery(id+"F0.wireOp",EDGE,"E2.10.6.0"),sQuery(id+"F0.wireOp",EDGE,"E2.10.7.0"),sQuery(id+"F0.wireOp",EDGE,"E2.10.8.0"),sQuery(id+"F0.wireOp",EDGE,"E2.10.9.0"),sQuery(id+"F0.wireOp",EDGE,"E2.10.10.0"),sQuery(id+"F0.wireOp",EDGE,"E2.10.11.0"),sQuery(id+"F0.wireOp",EDGE,"E2.10.12.0"),sQuery(id+"F0.wireOp",EDGE,"E2.10.13.0"),sQuery(id+"F0.wireOp",EDGE,"E2.10.14.0"),sQuery(id+"F0.wireOp",EDGE,"E2.10.15.0"),sQuery(id+"F0.wireOp",EDGE,"E2.11.0.0"),sQuery(id+"F0.wireOp",EDGE,"E2.11.1.0"),sQuery(id+"F0.wireOp",EDGE,"E2.11.2.0"),sQuery(id+"F0.wireOp",EDGE,"E2.11.3.0"),sQuery(id+"F0.wireOp",EDGE,"E2.11.4.0"),sQuery(id+"F0.wireOp",EDGE,"E2.11.5.0"),sQuery(id+"F0.wireOp",EDGE,"E2.11.6.0"),sQuery(id+"F0.wireOp",EDGE,"E2.11.7.0"),sQuery(id+"F0.wireOp",EDGE,"E2.11.8.0"),sQuery(id+"F0.wireOp",EDGE,"E2.11.9.0"),sQuery(id+"F0.wireOp",EDGE,"E2.11.10.0"),sQuery(id+"F0.wireOp",EDGE,"E2.11.11.0"),sQuery(id+"F0.wireOp",EDGE,"E2.11.12.0"),sQuery(id+"F0.wireOp",EDGE,"E2.11.13.0"),sQuery(id+"F0.wireOp",EDGE,"E2.11.14.0"),sQuery(id+"F0.wireOp",EDGE,"E2.11.15.0"),sQuery(id+"F0.wireOp",EDGE,"E2.12.0.0"),sQuery(id+"F0.wireOp",EDGE,"E2.12.1.0"),sQuery(id+"F0.wireOp",EDGE,"E2.12.2.0"),sQuery(id+"F0.wireOp",EDGE,"E2.12.3.0"),sQuery(id+"F0.wireOp",EDGE,"E2.12.4.0"),sQuery(id+"F0.wireOp",EDGE,"E2.12.5.0"),sQuery(id+"F0.wireOp",EDGE,"E2.12.6.0"),sQuery(id+"F0.wireOp",EDGE,"E2.12.7.0"),sQuery(id+"F0.wireOp",EDGE,"E2.12.8.0"),sQuery(id+"F0.wireOp",EDGE,"E2.12.9.0"),sQuery(id+"F0.wireOp",EDGE,"E2.12.10.0"),sQuery(id+"F0.wireOp",EDGE,"E2.12.11.0"),sQuery(id+"F0.wireOp",EDGE,"E2.12.12.0"),sQuery(id+"F0.wireOp",EDGE,"E2.12.13.0"),sQuery(id+"F0.wireOp",EDGE,"E2.12.14.0"),sQuery(id+"F0.wireOp",EDGE,"E2.12.15.0"),sQuery(id+"F0.wireOp",EDGE,"E2.13.0.0"),sQuery(id+"F0.wireOp",EDGE,"E2.13.1.0"),sQuery(id+"F0.wireOp",EDGE,"E2.13.2.0"),sQuery(id+"F0.wireOp",EDGE,"E2.13.3.0"),sQuery(id+"F0.wireOp",EDGE,"E2.13.4.0"),sQuery(id+"F0.wireOp",EDGE,"E2.13.5.0"),sQuery(id+"F0.wireOp",EDGE,"E2.13.6.0"),sQuery(id+"F0.wireOp",EDGE,"E2.13.7.0"),sQuery(id+"F0.wireOp",EDGE,"E2.13.8.0"),sQuery(id+"F0.wireOp",EDGE,"E2.13.9.0"),sQuery(id+"F0.wireOp",EDGE,"E2.13.10.0"),sQuery(id+"F0.wireOp",EDGE,"E2.13.11.0"),sQuery(id+"F0.wireOp",EDGE,"E2.13.12.0"),sQuery(id+"F0.wireOp",EDGE,"E2.13.13.0"),sQuery(id+"F0.wireOp",EDGE,"E2.13.14.0"),sQuery(id+"F0.wireOp",EDGE,"E2.13.15.0"),sQuery(id+"F0.wireOp",EDGE,"E2.14.0.0"),sQuery(id+"F0.wireOp",EDGE,"E2.14.1.0"),sQuery(id+"F0.wireOp",EDGE,"E2.14.2.0"),sQuery(id+"F0.wireOp",EDGE,"E2.14.3.0"),sQuery(id+"F0.wireOp",EDGE,"E2.14.4.0"),sQuery(id+"F0.wireOp",EDGE,"E2.14.5.0"),sQuery(id+"F0.wireOp",EDGE,"E2.14.6.0"),sQuery(id+"F0.wireOp",EDGE,"E2.14.7.0"),sQuery(id+"F0.wireOp",EDGE,"E2.14.8.0"),sQuery(id+"F0.wireOp",EDGE,"E2.14.9.0"),sQuery(id+"F0.wireOp",EDGE,"E2.14.10.0"),sQuery(id+"F0.wireOp",EDGE,"E2.14.11.0"),sQuery(id+"F0.wireOp",EDGE,"E2.14.12.0"),sQuery(id+"F0.wireOp",EDGE,"E2.14.13.0"),sQuery(id+"F0.wireOp",EDGE,"E2.14.14.0"),sQuery(id+"F0.wireOp",EDGE,"E2.14.15.0"),sQuery(id+"F0.wireOp",EDGE,"E2.15.0.0"),sQuery(id+"F0.wireOp",EDGE,"E2.15.1.0"),sQuery(id+"F0.wireOp",EDGE,"E2.15.2.0"),sQuery(id+"F0.wireOp",EDGE,"E2.15.3.0"),sQuery(id+"F0.wireOp",EDGE,"E2.15.4.0"),sQuery(id+"F0.wireOp",EDGE,"E2.15.5.0"),sQuery(id+"F0.wireOp",EDGE,"E2.15.6.0"),sQuery(id+"F0.wireOp",EDGE,"E2.15.7.0"),sQuery(id+"F0.wireOp",EDGE,"E2.15.8.0"),sQuery(id+"F0.wireOp",EDGE,"E2.15.9.0"),sQuery(id+"F0.wireOp",EDGE,"E2.15.10.0"),sQuery(id+"F0.wireOp",EDGE,"E2.15.11.0"),sQuery(id+"F0.wireOp",EDGE,"E2.15.12.0"),sQuery(id+"F0.wireOp",EDGE,"E2.15.13.0"),sQuery(id+"F0.wireOp",EDGE,"E2.15.14.0"),sQuery(id+"F0.wireOp",EDGE,"E2.15.15.0"),sQuery(id+"F0.wireOp",EDGE,"6f7ae5fc-1566-4385-bfb5-e6e9eca27b98.0.0.16"),sQuery(id+"F0.wireOp",EDGE,"6f7ae5fc-1566-4385-bfb5-e6e9eca27b98.0.1.16"),sQuery(id+"F0.wireOp",EDGE,"6f7ae5fc-1566-4385-bfb5-e6e9eca27b98.0.2.16"),sQuery(id+"F0.wireOp",EDGE,"6f7ae5fc-1566-4385-bfb5-e6e9eca27b98.0.3.16"),sQuery(id+"F0.wireOp",EDGE,"6f7ae5fc-1566-4385-bfb5-e6e9eca27b98.0.4.16"),sQuery(id+"F0.wireOp",EDGE,"6f7ae5fc-1566-4385-bfb5-e6e9eca27b98.0.5.16"),sQuery(id+"F0.wireOp",EDGE,"6f7ae5fc-1566-4385-bfb5-e6e9eca27b98.0.6.16"),sQuery(id+"F0.wireOp",EDGE,"6f7ae5fc-1566-4385-bfb5-e6e9eca27b98.0.7.16"),sQuery(id+"F0.wireOp",EDGE,"6f7ae5fc-1566-4385-bfb5-e6e9eca27b98.0.8.16"),sQuery(id+"F0.wireOp",EDGE,"6f7ae5fc-1566-4385-bfb5-e6e9eca27b98.0.9.16"),sQuery(id+"F0.wireOp",EDGE,"6f7ae5fc-1566-4385-bfb5-e6e9eca27b98.0.10.16"),sQuery(id+"F0.wireOp",EDGE,"6f7ae5fc-1566-4385-bfb5-e6e9eca27b98.0.11.16"),sQuery(id+"F0.wireOp",EDGE,"6f7ae5fc-1566-4385-bfb5-e6e9eca27b98.0.12.16"),sQuery(id+"F0.wireOp",EDGE,"6f7ae5fc-1566-4385-bfb5-e6e9eca27b98.0.13.16"),sQuery(id+"F0.wireOp",EDGE,"6f7ae5fc-1566-4385-bfb5-e6e9eca27b98.0.14.16"),sQuery(id+"F0.wireOp",EDGE,"6f7ae5fc-1566-4385-bfb5-e6e9eca27b98.0.15.16"),sQuery(id+"F0.wireOp",EDGE,"da7dbd3b-79dd-422c-88db-b753358300f9.0.16.0"),sQuery(id+"F0.wireOp",EDGE,"da7dbd3b-79dd-422c-88db-b753358300f9.0.16.1"),sQuery(id+"F0.wireOp",EDGE,"da7dbd3b-79dd-422c-88db-b753358300f9.0.16.2"),sQuery(id+"F0.wireOp",EDGE,"da7dbd3b-79dd-422c-88db-b753358300f9.0.16.3"),sQuery(id+"F0.wireOp",EDGE,"da7dbd3b-79dd-422c-88db-b753358300f9.0.16.4"),sQuery(id+"F0.wireOp",EDGE,"da7dbd3b-79dd-422c-88db-b753358300f9.0.16.5"),sQuery(id+"F0.wireOp",EDGE,"da7dbd3b-79dd-422c-88db-b753358300f9.0.16.6"),sQuery(id+"F0.wireOp",EDGE,"da7dbd3b-79dd-422c-88db-b753358300f9.0.16.7"),sQuery(id+"F0.wireOp",EDGE,"da7dbd3b-79dd-422c-88db-b753358300f9.0.16.8"),sQuery(id+"F0.wireOp",EDGE,"da7dbd3b-79dd-422c-88db-b753358300f9.0.16.9"),sQuery(id+"F0.wireOp",EDGE,"da7dbd3b-79dd-422c-88db-b753358300f9.0.16.10"),sQuery(id+"F0.wireOp",EDGE,"da7dbd3b-79dd-422c-88db-b753358300f9.0.16.11"),sQuery(id+"F0.wireOp",EDGE,"da7dbd3b-79dd-422c-88db-b753358300f9.0.16.12"),sQuery(id+"F0.wireOp",EDGE,"da7dbd3b-79dd-422c-88db-b753358300f9.0.16.13"),sQuery(id+"F0.wireOp",EDGE,"da7dbd3b-79dd-422c-88db-b753358300f9.0.16.14"),sQuery(id+"F0.wireOp",EDGE,"da7dbd3b-79dd-422c-88db-b753358300f9.0.16.15"),sQuery(id+"F0.wireOp",EDGE,"da7dbd3b-79dd-422c-88db-b753358300f9.0.16.16")])],"isStart":false});
            var sketch = newSketch(context, id + "F2", { "sketchPlane" : qUnion([Q0])});
            skLineSegment(sketch, "E6.bottom", {"start": v(-162.75, 114) * mm, "end": v(-161.25, 114) * mm});
            skLineSegment(sketch, "E6.left", {"start": v(-162.75, 114) * mm, "end": v(-162.75, -102.75) * mm});
            skLineSegment(sketch, "E6.right", {"start": v(-161.25, 114) * mm, "end": v(-161.25, -101.25) * mm});
            skLineSegment(sketch, "E7.bottom", {"start": v(174, -101.25) * mm, "end": v(-161.25, -101.25) * mm});
            skLineSegment(sketch, "E7.top", {"start": v(174, -102.75) * mm, "end": v(-162.75, -102.75) * mm});
            skLineSegment(sketch, "E7.left", {"start": v(174, -101.25) * mm, "end": v(174, -102.75) * mm});
            skSolve(sketch);
        }
        {
            var Q0;
            {var subQ0=sQuery(id+"F0.wireOp",EDGE,"E3.0.1.16");var subQ1=sQuery(id+"F0.wireOp",EDGE,"6f7ae5fc-1566-4385-bfb5-e6e9eca27b98.0.0.16");var subQ2=sQuery(id+"F0.wireOp",EDGE,"E2.0.8.0");var subQ3=sQuery(id+"F0.wireOp",EDGE,"E2.0.9.0");var subQ4=sQuery(id+"F0.wireOp",EDGE,"E2.0.15.0");var subQ5=sQuery(id+"F0.wireOp",EDGE,"E2.0.14.0");var subQ6=sQuery(id+"F0.wireOp",EDGE,"E2.0.6.0");var subQ7=sQuery(id+"F0.wireOp",EDGE,"E3.0.6.16");var subQ8=sQuery(id+"F0.wireOp",EDGE,"E3.0.9.16");var subQ9=sQuery(id+"F0.wireOp",EDGE,"E2.0.13.0");var subQ10=sQuery(id+"F0.wireOp",EDGE,"E2.0.11.0");var subQ11=sQuery(id+"F0.wireOp",EDGE,"E3.0.14.16");var subQ12=sQuery(id+"F0.wireOp",EDGE,"E2.0.7.0");var subQ13=sQuery(id+"F0.wireOp",EDGE,"E0.right");var subQ14=sQuery(id+"F0.wireOp",EDGE,"E3.0.8.16");var subQ15=sQuery(id+"F0.wireOp",EDGE,"E0.left");var subQ16=sQuery(id+"F0.wireOp",EDGE,"E0.top");var subQ17=sQuery(id+"F0.wireOp",EDGE,"E2.0.4.0");var subQ18=sQuery(id+"F0.wireOp",EDGE,"E2.0.12.0");var subQ19=sQuery(id+"F0.wireOp",EDGE,"E0.bottom");var subQ20=sQuery(id+"F0.wireOp",EDGE,"E1");var subQ21=sQuery(id+"F0.wireOp",EDGE,"E3.0.10.16");var subQ22=sQuery(id+"F0.wireOp",EDGE,"E2.0.1.0");var subQ23=sQuery(id+"F0.wireOp",EDGE,"E2.0.2.0");var subQ24=sQuery(id+"F0.wireOp",EDGE,"E2.0.10.0");var subQ25=sQuery(id+"F0.wireOp",EDGE,"E2.0.3.0");var subQ26=sQuery(id+"F0.wireOp",EDGE,"E3.0.2.16");var subQ27=sQuery(id+"F0.wireOp",EDGE,"E2.0.5.0");var subQ28=sQuery(id+"F0.wireOp",EDGE,"E3.0.3.16");var subQ29=sQuery(id+"F0.wireOp",EDGE,"E3.0.4.16");var subQ30=sQuery(id+"F0.wireOp",EDGE,"E3.0.5.16");var subQ31=sQuery(id+"F0.wireOp",EDGE,"E3.0.7.16");var subQ32=sQuery(id+"F0.wireOp",EDGE,"E3.0.11.16");var subQ33=sQuery(id+"F0.wireOp",EDGE,"E3.0.12.16");var subQ34=sQuery(id+"F0.wireOp",EDGE,"E3.0.13.16");var subQ35=sQuery(id+"F0.wireOp",EDGE,"E3.0.15.16");var subQ36=sQuery(id+"F0.wireOp",EDGE,"E3.0.16.16");Q0=makeQuery(id+"FJqtpdUANZnq3Um_1.boolean.opBoolean","SPLIT",FACE,{"disambiguationData":[TD([makeQuery(id+"F1.opExtrude","SWEPT_FACE",FACE,{"disambiguationData":[OSD([subQ19])]})])],"derivedFrom":makeQuery(id+"F1.opExtrude","CAP_FACE",FACE,{"disambiguationData":[OSD([subQ19,subQ16,subQ15,subQ13,subQ20,subQ22,subQ23,subQ25,subQ17,subQ27,subQ6,subQ12,subQ2,subQ3,subQ24,subQ10,subQ18,subQ9,subQ5,subQ4,subQ1,sQuery(id+"F0.wireOp",EDGE,"E3.0.1.0"),sQuery(id+"F0.wireOp",EDGE,"E3.0.1.1"),sQuery(id+"F0.wireOp",EDGE,"E3.0.1.2"),sQuery(id+"F0.wireOp",EDGE,"E3.0.1.3"),sQuery(id+"F0.wireOp",EDGE,"E3.0.1.4"),sQuery(id+"F0.wireOp",EDGE,"E3.0.1.5"),sQuery(id+"F0.wireOp",EDGE,"E3.0.1.6"),sQuery(id+"F0.wireOp",EDGE,"E3.0.1.7"),sQuery(id+"F0.wireOp",EDGE,"E3.0.1.8"),sQuery(id+"F0.wireOp",EDGE,"E3.0.1.9"),sQuery(id+"F0.wireOp",EDGE,"E3.0.1.10"),sQuery(id+"F0.wireOp",EDGE,"E3.0.1.11"),sQuery(id+"F0.wireOp",EDGE,"E3.0.1.12"),sQuery(id+"F0.wireOp",EDGE,"E3.0.1.13"),sQuery(id+"F0.wireOp",EDGE,"E3.0.1.14"),sQuery(id+"F0.wireOp",EDGE,"E3.0.1.15"),subQ0,sQuery(id+"F0.wireOp",EDGE,"E3.0.2.0"),sQuery(id+"F0.wireOp",EDGE,"E3.0.2.1"),sQuery(id+"F0.wireOp",EDGE,"E3.0.2.2"),sQuery(id+"F0.wireOp",EDGE,"E3.0.2.3"),sQuery(id+"F0.wireOp",EDGE,"E3.0.2.4"),sQuery(id+"F0.wireOp",EDGE,"E3.0.2.5"),sQuery(id+"F0.wireOp",EDGE,"E3.0.2.6"),sQuery(id+"F0.wireOp",EDGE,"E3.0.2.7"),sQuery(id+"F0.wireOp",EDGE,"E3.0.2.8"),sQuery(id+"F0.wireOp",EDGE,"E3.0.2.9"),sQuery(id+"F0.wireOp",EDGE,"E3.0.2.10"),sQuery(id+"F0.wireOp",EDGE,"E3.0.2.11"),sQuery(id+"F0.wireOp",EDGE,"E3.0.2.12"),sQuery(id+"F0.wireOp",EDGE,"E3.0.2.13"),sQuery(id+"F0.wireOp",EDGE,"E3.0.2.14"),sQuery(id+"F0.wireOp",EDGE,"E3.0.2.15"),subQ26,sQuery(id+"F0.wireOp",EDGE,"E3.0.3.0"),sQuery(id+"F0.wireOp",EDGE,"E3.0.3.1"),sQuery(id+"F0.wireOp",EDGE,"E3.0.3.2"),sQuery(id+"F0.wireOp",EDGE,"E3.0.3.3"),sQuery(id+"F0.wireOp",EDGE,"E3.0.3.4"),sQuery(id+"F0.wireOp",EDGE,"E3.0.3.5"),sQuery(id+"F0.wireOp",EDGE,"E3.0.3.6"),sQuery(id+"F0.wireOp",EDGE,"E3.0.3.7"),sQuery(id+"F0.wireOp",EDGE,"E3.0.3.8"),sQuery(id+"F0.wireOp",EDGE,"E3.0.3.9"),sQuery(id+"F0.wireOp",EDGE,"E3.0.3.10"),sQuery(id+"F0.wireOp",EDGE,"E3.0.3.11"),sQuery(id+"F0.wireOp",EDGE,"E3.0.3.12"),sQuery(id+"F0.wireOp",EDGE,"E3.0.3.13"),sQuery(id+"F0.wireOp",EDGE,"E3.0.3.14"),sQuery(id+"F0.wireOp",EDGE,"E3.0.3.15"),subQ28,sQuery(id+"F0.wireOp",EDGE,"E3.0.4.0"),sQuery(id+"F0.wireOp",EDGE,"E3.0.4.1"),sQuery(id+"F0.wireOp",EDGE,"E3.0.4.2"),sQuery(id+"F0.wireOp",EDGE,"E3.0.4.3"),sQuery(id+"F0.wireOp",EDGE,"E3.0.4.4"),sQuery(id+"F0.wireOp",EDGE,"E3.0.4.5"),sQuery(id+"F0.wireOp",EDGE,"E3.0.4.6"),sQuery(id+"F0.wireOp",EDGE,"E3.0.4.7"),sQuery(id+"F0.wireOp",EDGE,"E3.0.4.8"),sQuery(id+"F0.wireOp",EDGE,"E3.0.4.9"),sQuery(id+"F0.wireOp",EDGE,"E3.0.4.10"),sQuery(id+"F0.wireOp",EDGE,"E3.0.4.11"),sQuery(id+"F0.wireOp",EDGE,"E3.0.4.12"),sQuery(id+"F0.wireOp",EDGE,"E3.0.4.13"),sQuery(id+"F0.wireOp",EDGE,"E3.0.4.14"),sQuery(id+"F0.wireOp",EDGE,"E3.0.4.15"),subQ29,sQuery(id+"F0.wireOp",EDGE,"E3.0.5.0"),sQuery(id+"F0.wireOp",EDGE,"E3.0.5.1"),sQuery(id+"F0.wireOp",EDGE,"E3.0.5.2"),sQuery(id+"F0.wireOp",EDGE,"E3.0.5.3"),sQuery(id+"F0.wireOp",EDGE,"E3.0.5.4"),sQuery(id+"F0.wireOp",EDGE,"E3.0.5.5"),sQuery(id+"F0.wireOp",EDGE,"E3.0.5.6"),sQuery(id+"F0.wireOp",EDGE,"E3.0.5.7"),sQuery(id+"F0.wireOp",EDGE,"E3.0.5.8"),sQuery(id+"F0.wireOp",EDGE,"E3.0.5.9"),sQuery(id+"F0.wireOp",EDGE,"E3.0.5.10"),sQuery(id+"F0.wireOp",EDGE,"E3.0.5.11"),sQuery(id+"F0.wireOp",EDGE,"E3.0.5.12"),sQuery(id+"F0.wireOp",EDGE,"E3.0.5.13"),sQuery(id+"F0.wireOp",EDGE,"E3.0.5.14"),sQuery(id+"F0.wireOp",EDGE,"E3.0.5.15"),subQ30,sQuery(id+"F0.wireOp",EDGE,"E3.0.6.0"),sQuery(id+"F0.wireOp",EDGE,"E3.0.6.1"),sQuery(id+"F0.wireOp",EDGE,"E3.0.6.2"),sQuery(id+"F0.wireOp",EDGE,"E3.0.6.3"),sQuery(id+"F0.wireOp",EDGE,"E3.0.6.4"),sQuery(id+"F0.wireOp",EDGE,"E3.0.6.5"),sQuery(id+"F0.wireOp",EDGE,"E3.0.6.6"),sQuery(id+"F0.wireOp",EDGE,"E3.0.6.7"),sQuery(id+"F0.wireOp",EDGE,"E3.0.6.8"),sQuery(id+"F0.wireOp",EDGE,"E3.0.6.9"),sQuery(id+"F0.wireOp",EDGE,"E3.0.6.10"),sQuery(id+"F0.wireOp",EDGE,"E3.0.6.11"),sQuery(id+"F0.wireOp",EDGE,"E3.0.6.12"),sQuery(id+"F0.wireOp",EDGE,"E3.0.6.13"),sQuery(id+"F0.wireOp",EDGE,"E3.0.6.14"),sQuery(id+"F0.wireOp",EDGE,"E3.0.6.15"),subQ7,sQuery(id+"F0.wireOp",EDGE,"E3.0.7.0"),sQuery(id+"F0.wireOp",EDGE,"E3.0.7.1"),sQuery(id+"F0.wireOp",EDGE,"E3.0.7.2"),sQuery(id+"F0.wireOp",EDGE,"E3.0.7.3"),sQuery(id+"F0.wireOp",EDGE,"E3.0.7.4"),sQuery(id+"F0.wireOp",EDGE,"E3.0.7.5"),sQuery(id+"F0.wireOp",EDGE,"E3.0.7.6"),sQuery(id+"F0.wireOp",EDGE,"E3.0.7.7"),sQuery(id+"F0.wireOp",EDGE,"E3.0.7.8"),sQuery(id+"F0.wireOp",EDGE,"E3.0.7.9"),sQuery(id+"F0.wireOp",EDGE,"E3.0.7.10"),sQuery(id+"F0.wireOp",EDGE,"E3.0.7.11"),sQuery(id+"F0.wireOp",EDGE,"E3.0.7.12"),sQuery(id+"F0.wireOp",EDGE,"E3.0.7.13"),sQuery(id+"F0.wireOp",EDGE,"E3.0.7.14"),sQuery(id+"F0.wireOp",EDGE,"E3.0.7.15"),subQ31,sQuery(id+"F0.wireOp",EDGE,"E3.0.8.0"),sQuery(id+"F0.wireOp",EDGE,"E3.0.8.1"),sQuery(id+"F0.wireOp",EDGE,"E3.0.8.2"),sQuery(id+"F0.wireOp",EDGE,"E3.0.8.3"),sQuery(id+"F0.wireOp",EDGE,"E3.0.8.4"),sQuery(id+"F0.wireOp",EDGE,"E3.0.8.5"),sQuery(id+"F0.wireOp",EDGE,"E3.0.8.6"),sQuery(id+"F0.wireOp",EDGE,"E3.0.8.7"),sQuery(id+"F0.wireOp",EDGE,"E3.0.8.8"),sQuery(id+"F0.wireOp",EDGE,"E3.0.8.9"),sQuery(id+"F0.wireOp",EDGE,"E3.0.8.10"),sQuery(id+"F0.wireOp",EDGE,"E3.0.8.11"),sQuery(id+"F0.wireOp",EDGE,"E3.0.8.12"),sQuery(id+"F0.wireOp",EDGE,"E3.0.8.13"),sQuery(id+"F0.wireOp",EDGE,"E3.0.8.14"),sQuery(id+"F0.wireOp",EDGE,"E3.0.8.15"),subQ14,sQuery(id+"F0.wireOp",EDGE,"E3.0.9.0"),sQuery(id+"F0.wireOp",EDGE,"E3.0.9.1"),sQuery(id+"F0.wireOp",EDGE,"E3.0.9.2"),sQuery(id+"F0.wireOp",EDGE,"E3.0.9.3"),sQuery(id+"F0.wireOp",EDGE,"E3.0.9.4"),sQuery(id+"F0.wireOp",EDGE,"E3.0.9.5"),sQuery(id+"F0.wireOp",EDGE,"E3.0.9.6"),sQuery(id+"F0.wireOp",EDGE,"E3.0.9.7"),sQuery(id+"F0.wireOp",EDGE,"E3.0.9.8"),sQuery(id+"F0.wireOp",EDGE,"E3.0.9.9"),sQuery(id+"F0.wireOp",EDGE,"E3.0.9.10"),sQuery(id+"F0.wireOp",EDGE,"E3.0.9.11"),sQuery(id+"F0.wireOp",EDGE,"E3.0.9.12"),sQuery(id+"F0.wireOp",EDGE,"E3.0.9.13"),sQuery(id+"F0.wireOp",EDGE,"E3.0.9.14"),sQuery(id+"F0.wireOp",EDGE,"E3.0.9.15"),subQ8,sQuery(id+"F0.wireOp",EDGE,"E3.0.10.0"),sQuery(id+"F0.wireOp",EDGE,"E3.0.10.1"),sQuery(id+"F0.wireOp",EDGE,"E3.0.10.2"),sQuery(id+"F0.wireOp",EDGE,"E3.0.10.3"),sQuery(id+"F0.wireOp",EDGE,"E3.0.10.4"),sQuery(id+"F0.wireOp",EDGE,"E3.0.10.5"),sQuery(id+"F0.wireOp",EDGE,"E3.0.10.6"),sQuery(id+"F0.wireOp",EDGE,"E3.0.10.7"),sQuery(id+"F0.wireOp",EDGE,"E3.0.10.8"),sQuery(id+"F0.wireOp",EDGE,"E3.0.10.9"),sQuery(id+"F0.wireOp",EDGE,"E3.0.10.10"),sQuery(id+"F0.wireOp",EDGE,"E3.0.10.11"),sQuery(id+"F0.wireOp",EDGE,"E3.0.10.12"),sQuery(id+"F0.wireOp",EDGE,"E3.0.10.13"),sQuery(id+"F0.wireOp",EDGE,"E3.0.10.14"),sQuery(id+"F0.wireOp",EDGE,"E3.0.10.15"),subQ21,sQuery(id+"F0.wireOp",EDGE,"E3.0.11.0"),sQuery(id+"F0.wireOp",EDGE,"E3.0.11.1"),sQuery(id+"F0.wireOp",EDGE,"E3.0.11.2"),sQuery(id+"F0.wireOp",EDGE,"E3.0.11.3"),sQuery(id+"F0.wireOp",EDGE,"E3.0.11.4"),sQuery(id+"F0.wireOp",EDGE,"E3.0.11.5"),sQuery(id+"F0.wireOp",EDGE,"E3.0.11.6"),sQuery(id+"F0.wireOp",EDGE,"E3.0.11.7"),sQuery(id+"F0.wireOp",EDGE,"E3.0.11.8"),sQuery(id+"F0.wireOp",EDGE,"E3.0.11.9"),sQuery(id+"F0.wireOp",EDGE,"E3.0.11.10"),sQuery(id+"F0.wireOp",EDGE,"E3.0.11.11"),sQuery(id+"F0.wireOp",EDGE,"E3.0.11.12"),sQuery(id+"F0.wireOp",EDGE,"E3.0.11.13"),sQuery(id+"F0.wireOp",EDGE,"E3.0.11.14"),sQuery(id+"F0.wireOp",EDGE,"E3.0.11.15"),subQ32,sQuery(id+"F0.wireOp",EDGE,"E3.0.12.0"),sQuery(id+"F0.wireOp",EDGE,"E3.0.12.1"),sQuery(id+"F0.wireOp",EDGE,"E3.0.12.2"),sQuery(id+"F0.wireOp",EDGE,"E3.0.12.3"),sQuery(id+"F0.wireOp",EDGE,"E3.0.12.4"),sQuery(id+"F0.wireOp",EDGE,"E3.0.12.5"),sQuery(id+"F0.wireOp",EDGE,"E3.0.12.6"),sQuery(id+"F0.wireOp",EDGE,"E3.0.12.7"),sQuery(id+"F0.wireOp",EDGE,"E3.0.12.8"),sQuery(id+"F0.wireOp",EDGE,"E3.0.12.9"),sQuery(id+"F0.wireOp",EDGE,"E3.0.12.10"),sQuery(id+"F0.wireOp",EDGE,"E3.0.12.11"),sQuery(id+"F0.wireOp",EDGE,"E3.0.12.12"),sQuery(id+"F0.wireOp",EDGE,"E3.0.12.13"),sQuery(id+"F0.wireOp",EDGE,"E3.0.12.14"),sQuery(id+"F0.wireOp",EDGE,"E3.0.12.15"),subQ33,sQuery(id+"F0.wireOp",EDGE,"E3.0.13.0"),sQuery(id+"F0.wireOp",EDGE,"E3.0.13.1"),sQuery(id+"F0.wireOp",EDGE,"E3.0.13.2"),sQuery(id+"F0.wireOp",EDGE,"E3.0.13.3"),sQuery(id+"F0.wireOp",EDGE,"E3.0.13.4"),sQuery(id+"F0.wireOp",EDGE,"E3.0.13.5"),sQuery(id+"F0.wireOp",EDGE,"E3.0.13.6"),sQuery(id+"F0.wireOp",EDGE,"E3.0.13.7"),sQuery(id+"F0.wireOp",EDGE,"E3.0.13.8"),sQuery(id+"F0.wireOp",EDGE,"E3.0.13.9"),sQuery(id+"F0.wireOp",EDGE,"E3.0.13.10"),sQuery(id+"F0.wireOp",EDGE,"E3.0.13.11"),sQuery(id+"F0.wireOp",EDGE,"E3.0.13.12"),sQuery(id+"F0.wireOp",EDGE,"E3.0.13.13"),sQuery(id+"F0.wireOp",EDGE,"E3.0.13.14"),sQuery(id+"F0.wireOp",EDGE,"E3.0.13.15"),subQ34,sQuery(id+"F0.wireOp",EDGE,"E3.0.14.0"),sQuery(id+"F0.wireOp",EDGE,"E3.0.14.1"),sQuery(id+"F0.wireOp",EDGE,"E3.0.14.2"),sQuery(id+"F0.wireOp",EDGE,"E3.0.14.3"),sQuery(id+"F0.wireOp",EDGE,"E3.0.14.4"),sQuery(id+"F0.wireOp",EDGE,"E3.0.14.5"),sQuery(id+"F0.wireOp",EDGE,"E3.0.14.6"),sQuery(id+"F0.wireOp",EDGE,"E3.0.14.7"),sQuery(id+"F0.wireOp",EDGE,"E3.0.14.8"),sQuery(id+"F0.wireOp",EDGE,"E3.0.14.9"),sQuery(id+"F0.wireOp",EDGE,"E3.0.14.10"),sQuery(id+"F0.wireOp",EDGE,"E3.0.14.11"),sQuery(id+"F0.wireOp",EDGE,"E3.0.14.12"),sQuery(id+"F0.wireOp",EDGE,"E3.0.14.13"),sQuery(id+"F0.wireOp",EDGE,"E3.0.14.14"),sQuery(id+"F0.wireOp",EDGE,"E3.0.14.15"),subQ11,sQuery(id+"F0.wireOp",EDGE,"E3.0.15.0"),sQuery(id+"F0.wireOp",EDGE,"E3.0.15.1"),sQuery(id+"F0.wireOp",EDGE,"E3.0.15.2"),sQuery(id+"F0.wireOp",EDGE,"E3.0.15.3"),sQuery(id+"F0.wireOp",EDGE,"E3.0.15.4"),sQuery(id+"F0.wireOp",EDGE,"E3.0.15.5"),sQuery(id+"F0.wireOp",EDGE,"E3.0.15.6"),sQuery(id+"F0.wireOp",EDGE,"E3.0.15.7"),sQuery(id+"F0.wireOp",EDGE,"E3.0.15.8"),sQuery(id+"F0.wireOp",EDGE,"E3.0.15.9"),sQuery(id+"F0.wireOp",EDGE,"E3.0.15.10"),sQuery(id+"F0.wireOp",EDGE,"E3.0.15.11"),sQuery(id+"F0.wireOp",EDGE,"E3.0.15.12"),sQuery(id+"F0.wireOp",EDGE,"E3.0.15.13"),sQuery(id+"F0.wireOp",EDGE,"E3.0.15.14"),sQuery(id+"F0.wireOp",EDGE,"E3.0.15.15"),subQ35,sQuery(id+"F0.wireOp",EDGE,"E3.0.16.0"),sQuery(id+"F0.wireOp",EDGE,"E3.0.16.1"),sQuery(id+"F0.wireOp",EDGE,"E3.0.16.2"),sQuery(id+"F0.wireOp",EDGE,"E3.0.16.3"),sQuery(id+"F0.wireOp",EDGE,"E3.0.16.4"),sQuery(id+"F0.wireOp",EDGE,"E3.0.16.5"),sQuery(id+"F0.wireOp",EDGE,"E3.0.16.6"),sQuery(id+"F0.wireOp",EDGE,"E3.0.16.7"),sQuery(id+"F0.wireOp",EDGE,"E3.0.16.8"),sQuery(id+"F0.wireOp",EDGE,"E3.0.16.9"),sQuery(id+"F0.wireOp",EDGE,"E3.0.16.10"),sQuery(id+"F0.wireOp",EDGE,"E3.0.16.11"),sQuery(id+"F0.wireOp",EDGE,"E3.0.16.12"),sQuery(id+"F0.wireOp",EDGE,"E3.0.16.13"),sQuery(id+"F0.wireOp",EDGE,"E3.0.16.14"),sQuery(id+"F0.wireOp",EDGE,"E3.0.16.15"),subQ36])],"isStart":false})});}
            var sketch = newSketch(context, id + "F3", { "sketchPlane" : qUnion([Q0])});
            skLineSegment(sketch, "E8.bottom", {"start": v(-150.75, -102) * mm, "end": v(-149.25, -102) * mm});
            skLineSegment(sketch, "E8.top", {"start": v(-150.75, -108) * mm, "end": v(-149.25, -108) * mm});
            skLineSegment(sketch, "E8.left", {"start": v(-150.75, -102) * mm, "end": v(-150.75, -108) * mm});
            skLineSegment(sketch, "E8.right", {"start": v(-149.25, -102) * mm, "end": v(-149.25, -108) * mm});
            skLineSegment(sketch, "E9.1.0.0", {"start": v(-138.75, -102) * mm, "end": v(-138.75, -108) * mm});
            skLineSegment(sketch, "E9.1.0.1", {"start": v(-138.75, -102) * mm, "end": v(-137.25, -102) * mm});
            skLineSegment(sketch, "E9.1.0.2", {"start": v(-137.25, -102) * mm, "end": v(-137.25, -108) * mm});
            skLineSegment(sketch, "E9.1.0.3", {"start": v(-138.75, -108) * mm, "end": v(-137.25, -108) * mm});
            skLineSegment(sketch, "E9.2.0.0", {"start": v(-126.75, -102) * mm, "end": v(-126.75, -108) * mm});
            skLineSegment(sketch, "E9.2.0.1", {"start": v(-126.75, -102) * mm, "end": v(-125.25, -102) * mm});
            skLineSegment(sketch, "E9.2.0.2", {"start": v(-125.25, -102) * mm, "end": v(-125.25, -108) * mm});
            skLineSegment(sketch, "E9.2.0.3", {"start": v(-126.75, -108) * mm, "end": v(-125.25, -108) * mm});
            skLineSegment(sketch, "E9.3.0.0", {"start": v(-114.75, -102) * mm, "end": v(-114.75, -108) * mm});
            skLineSegment(sketch, "E9.3.0.1", {"start": v(-114.75, -102) * mm, "end": v(-113.25, -102) * mm});
            skLineSegment(sketch, "E9.3.0.2", {"start": v(-113.25, -102) * mm, "end": v(-113.25, -108) * mm});
            skLineSegment(sketch, "E9.3.0.3", {"start": v(-114.75, -108) * mm, "end": v(-113.25, -108) * mm});
            skLineSegment(sketch, "E9.4.0.0", {"start": v(-102.75, -102) * mm, "end": v(-102.75, -108) * mm});
            skLineSegment(sketch, "E9.4.0.1", {"start": v(-102.75, -102) * mm, "end": v(-101.25, -102) * mm});
            skLineSegment(sketch, "E9.4.0.2", {"start": v(-101.25, -102) * mm, "end": v(-101.25, -108) * mm});
            skLineSegment(sketch, "E9.4.0.3", {"start": v(-102.75, -108) * mm, "end": v(-101.25, -108) * mm});
            skLineSegment(sketch, "E9.5.0.0", {"start": v(-90.75, -102) * mm, "end": v(-90.75, -108) * mm});
            skLineSegment(sketch, "E9.5.0.1", {"start": v(-90.75, -102) * mm, "end": v(-89.25, -102) * mm});
            skLineSegment(sketch, "E9.5.0.2", {"start": v(-89.25, -102) * mm, "end": v(-89.25, -108) * mm});
            skLineSegment(sketch, "E9.5.0.3", {"start": v(-90.75, -108) * mm, "end": v(-89.25, -108) * mm});
            skLineSegment(sketch, "E9.6.0.0", {"start": v(-78.75, -102) * mm, "end": v(-78.75, -108) * mm});
            skLineSegment(sketch, "E9.6.0.1", {"start": v(-78.75, -102) * mm, "end": v(-77.25, -102) * mm});
            skLineSegment(sketch, "E9.6.0.2", {"start": v(-77.25, -102) * mm, "end": v(-77.25, -108) * mm});
            skLineSegment(sketch, "E9.6.0.3", {"start": v(-78.75, -108) * mm, "end": v(-77.25, -108) * mm});
            skLineSegment(sketch, "E9.7.0.0", {"start": v(-66.75, -102) * mm, "end": v(-66.75, -108) * mm});
            skLineSegment(sketch, "E9.7.0.1", {"start": v(-66.75, -102) * mm, "end": v(-65.25, -102) * mm});
            skLineSegment(sketch, "E9.7.0.2", {"start": v(-65.25, -102) * mm, "end": v(-65.25, -108) * mm});
            skLineSegment(sketch, "E9.7.0.3", {"start": v(-66.75, -108) * mm, "end": v(-65.25, -108) * mm});
            skLineSegment(sketch, "E9.8.0.0", {"start": v(-54.75, -102) * mm, "end": v(-54.75, -108) * mm});
            skLineSegment(sketch, "E9.8.0.1", {"start": v(-54.75, -102) * mm, "end": v(-53.25, -102) * mm});
            skLineSegment(sketch, "E9.8.0.2", {"start": v(-53.25, -102) * mm, "end": v(-53.25, -108) * mm});
            skLineSegment(sketch, "E9.8.0.3", {"start": v(-54.75, -108) * mm, "end": v(-53.25, -108) * mm});
            skLineSegment(sketch, "E9.9.0.0", {"start": v(-42.75, -102) * mm, "end": v(-42.75, -108) * mm});
            skLineSegment(sketch, "E9.9.0.1", {"start": v(-42.75, -102) * mm, "end": v(-41.25, -102) * mm});
            skLineSegment(sketch, "E9.9.0.2", {"start": v(-41.25, -102) * mm, "end": v(-41.25, -108) * mm});
            skLineSegment(sketch, "E9.9.0.3", {"start": v(-42.75, -108) * mm, "end": v(-41.25, -108) * mm});
            skLineSegment(sketch, "E9.10.0.0", {"start": v(-30.75, -102) * mm, "end": v(-30.75, -108) * mm});
            skLineSegment(sketch, "E9.10.0.1", {"start": v(-30.75, -102) * mm, "end": v(-29.25, -102) * mm});
            skLineSegment(sketch, "E9.10.0.2", {"start": v(-29.25, -102) * mm, "end": v(-29.25, -108) * mm});
            skLineSegment(sketch, "E9.10.0.3", {"start": v(-30.75, -108) * mm, "end": v(-29.25, -108) * mm});
            skLineSegment(sketch, "E9.11.0.0", {"start": v(-18.75, -102) * mm, "end": v(-18.75, -108) * mm});
            skLineSegment(sketch, "E9.11.0.1", {"start": v(-18.75, -102) * mm, "end": v(-17.25, -102) * mm});
            skLineSegment(sketch, "E9.11.0.2", {"start": v(-17.25, -102) * mm, "end": v(-17.25, -108) * mm});
            skLineSegment(sketch, "E9.11.0.3", {"start": v(-18.75, -108) * mm, "end": v(-17.25, -108) * mm});
            skLineSegment(sketch, "E9.12.0.0", {"start": v(-6.75, -102) * mm, "end": v(-6.75, -108) * mm});
            skLineSegment(sketch, "E9.12.0.1", {"start": v(-6.75, -102) * mm, "end": v(-5.25, -102) * mm});
            skLineSegment(sketch, "E9.12.0.2", {"start": v(-5.25, -102) * mm, "end": v(-5.25, -108) * mm});
            skLineSegment(sketch, "E9.12.0.3", {"start": v(-6.75, -108) * mm, "end": v(-5.25, -108) * mm});
            skLineSegment(sketch, "E9.13.0.0", {"start": v(5.25, -102) * mm, "end": v(5.25, -108) * mm});
            skLineSegment(sketch, "E9.13.0.1", {"start": v(5.25, -102) * mm, "end": v(6.75, -102) * mm});
            skLineSegment(sketch, "E9.13.0.2", {"start": v(6.75, -102) * mm, "end": v(6.75, -108) * mm});
            skLineSegment(sketch, "E9.13.0.3", {"start": v(5.25, -108) * mm, "end": v(6.75, -108) * mm});
            skLineSegment(sketch, "E9.direction1", {"start": v(-150.75, -108) * mm, "end": v(-138.75, -108) * mm, "construction": true});
            skLineSegment(sketch, "E10.bottom", {"start": v(-162, -89.25) * mm, "end": v(-168, -89.25) * mm});
            skLineSegment(sketch, "E10.top", {"start": v(-162, -90.75) * mm, "end": v(-168, -90.75) * mm});
            skLineSegment(sketch, "E10.left", {"start": v(-162, -89.25) * mm, "end": v(-162, -90.75) * mm});
            skLineSegment(sketch, "E10.right", {"start": v(-168, -89.25) * mm, "end": v(-168, -90.75) * mm});
            skLineSegment(sketch, "E11.0.1.0", {"start": v(-168, -77.25) * mm, "end": v(-168, -78.75) * mm});
            skLineSegment(sketch, "E11.0.1.1", {"start": v(-162, -77.25) * mm, "end": v(-168, -77.25) * mm});
            skLineSegment(sketch, "E11.0.1.2", {"start": v(-162, -78.75) * mm, "end": v(-168, -78.75) * mm});
            skLineSegment(sketch, "E11.0.1.3", {"start": v(-162, -77.25) * mm, "end": v(-162, -78.75) * mm});
            skLineSegment(sketch, "E11.0.2.0", {"start": v(-168, -65.25) * mm, "end": v(-168, -66.75) * mm});
            skLineSegment(sketch, "E11.0.2.1", {"start": v(-162, -65.25) * mm, "end": v(-168, -65.25) * mm});
            skLineSegment(sketch, "E11.0.2.2", {"start": v(-162, -66.75) * mm, "end": v(-168, -66.75) * mm});
            skLineSegment(sketch, "E11.0.2.3", {"start": v(-162, -65.25) * mm, "end": v(-162, -66.75) * mm});
            skLineSegment(sketch, "E11.0.3.0", {"start": v(-168, -53.25) * mm, "end": v(-168, -54.75) * mm});
            skLineSegment(sketch, "E11.0.3.1", {"start": v(-162, -53.25) * mm, "end": v(-168, -53.25) * mm});
            skLineSegment(sketch, "E11.0.3.2", {"start": v(-162, -54.75) * mm, "end": v(-168, -54.75) * mm});
            skLineSegment(sketch, "E11.0.3.3", {"start": v(-162, -53.25) * mm, "end": v(-162, -54.75) * mm});
            skLineSegment(sketch, "E11.0.4.0", {"start": v(-168, -41.25) * mm, "end": v(-168, -42.75) * mm});
            skLineSegment(sketch, "E11.0.4.1", {"start": v(-162, -41.25) * mm, "end": v(-168, -41.25) * mm});
            skLineSegment(sketch, "E11.0.4.2", {"start": v(-162, -42.75) * mm, "end": v(-168, -42.75) * mm});
            skLineSegment(sketch, "E11.0.4.3", {"start": v(-162, -41.25) * mm, "end": v(-162, -42.75) * mm});
            skLineSegment(sketch, "E11.0.5.0", {"start": v(-168, -29.25) * mm, "end": v(-168, -30.75) * mm});
            skLineSegment(sketch, "E11.0.5.1", {"start": v(-162, -29.25) * mm, "end": v(-168, -29.25) * mm});
            skLineSegment(sketch, "E11.0.5.2", {"start": v(-162, -30.75) * mm, "end": v(-168, -30.75) * mm});
            skLineSegment(sketch, "E11.0.5.3", {"start": v(-162, -29.25) * mm, "end": v(-162, -30.75) * mm});
            skLineSegment(sketch, "E11.0.6.0", {"start": v(-168, -17.25) * mm, "end": v(-168, -18.75) * mm});
            skLineSegment(sketch, "E11.0.6.1", {"start": v(-162, -17.25) * mm, "end": v(-168, -17.25) * mm});
            skLineSegment(sketch, "E11.0.6.2", {"start": v(-162, -18.75) * mm, "end": v(-168, -18.75) * mm});
            skLineSegment(sketch, "E11.0.6.3", {"start": v(-162, -17.25) * mm, "end": v(-162, -18.75) * mm});
            skLineSegment(sketch, "E11.0.7.0", {"start": v(-168, -5.25) * mm, "end": v(-168, -6.75) * mm});
            skLineSegment(sketch, "E11.0.7.1", {"start": v(-162, -5.25) * mm, "end": v(-168, -5.25) * mm});
            skLineSegment(sketch, "E11.0.7.2", {"start": v(-162, -6.75) * mm, "end": v(-168, -6.75) * mm});
            skLineSegment(sketch, "E11.0.7.3", {"start": v(-162, -5.25) * mm, "end": v(-162, -6.75) * mm});
            skLineSegment(sketch, "E11.0.8.0", {"start": v(-168, 6.75) * mm, "end": v(-168, 5.25) * mm});
            skLineSegment(sketch, "E11.0.8.1", {"start": v(-162, 6.75) * mm, "end": v(-168, 6.75) * mm});
            skLineSegment(sketch, "E11.0.8.2", {"start": v(-162, 5.25) * mm, "end": v(-168, 5.25) * mm});
            skLineSegment(sketch, "E11.0.8.3", {"start": v(-162, 6.75) * mm, "end": v(-162, 5.25) * mm});
            skLineSegment(sketch, "E11.0.9.0", {"start": v(-168, 18.75) * mm, "end": v(-168, 17.25) * mm});
            skLineSegment(sketch, "E11.0.9.1", {"start": v(-162, 18.75) * mm, "end": v(-168, 18.75) * mm});
            skLineSegment(sketch, "E11.0.9.2", {"start": v(-162, 17.25) * mm, "end": v(-168, 17.25) * mm});
            skLineSegment(sketch, "E11.0.9.3", {"start": v(-162, 18.75) * mm, "end": v(-162, 17.25) * mm});
            skLineSegment(sketch, "E11.0.10.0", {"start": v(-168, 30.75) * mm, "end": v(-168, 29.25) * mm});
            skLineSegment(sketch, "E11.0.10.1", {"start": v(-162, 30.75) * mm, "end": v(-168, 30.75) * mm});
            skLineSegment(sketch, "E11.0.10.2", {"start": v(-162, 29.25) * mm, "end": v(-168, 29.25) * mm});
            skLineSegment(sketch, "E11.0.10.3", {"start": v(-162, 30.75) * mm, "end": v(-162, 29.25) * mm});
            skLineSegment(sketch, "E11.0.11.0", {"start": v(-168, 42.75) * mm, "end": v(-168, 41.25) * mm});
            skLineSegment(sketch, "E11.0.11.1", {"start": v(-162, 42.75) * mm, "end": v(-168, 42.75) * mm});
            skLineSegment(sketch, "E11.0.11.2", {"start": v(-162, 41.25) * mm, "end": v(-168, 41.25) * mm});
            skLineSegment(sketch, "E11.0.11.3", {"start": v(-162, 42.75) * mm, "end": v(-162, 41.25) * mm});
            skLineSegment(sketch, "E11.0.12.0", {"start": v(-168, 54.75) * mm, "end": v(-168, 53.25) * mm});
            skLineSegment(sketch, "E11.0.12.1", {"start": v(-162, 54.75) * mm, "end": v(-168, 54.75) * mm});
            skLineSegment(sketch, "E11.0.12.2", {"start": v(-162, 53.25) * mm, "end": v(-168, 53.25) * mm});
            skLineSegment(sketch, "E11.0.12.3", {"start": v(-162, 54.75) * mm, "end": v(-162, 53.25) * mm});
            skLineSegment(sketch, "E11.0.13.0", {"start": v(-168, 66.75) * mm, "end": v(-168, 65.25) * mm});
            skLineSegment(sketch, "E11.0.13.1", {"start": v(-162, 66.75) * mm, "end": v(-168, 66.75) * mm});
            skLineSegment(sketch, "E11.0.13.2", {"start": v(-162, 65.25) * mm, "end": v(-168, 65.25) * mm});
            skLineSegment(sketch, "E11.0.13.3", {"start": v(-162, 66.75) * mm, "end": v(-162, 65.25) * mm});
            skLineSegment(sketch, "E11.direction1", {"start": v(-168, -90.75) * mm, "end": v(-57.74, -90.75) * mm, "construction": true});
            skLineSegment(sketch, "E11.direction2", {"start": v(-168, -90.75) * mm, "end": v(-168, -78.75) * mm, "construction": true});
            skLineSegment(sketch, "E12.0.1.0", {"start": v(-162, 78.75) * mm, "end": v(-168, 78.75) * mm});
            skLineSegment(sketch, "E12.0.1.1", {"start": v(-162, 77.25) * mm, "end": v(-168, 77.25) * mm});
            skLineSegment(sketch, "E12.0.1.2", {"start": v(-168, 78.75) * mm, "end": v(-168, 77.25) * mm});
            skLineSegment(sketch, "E12.0.1.3", {"start": v(-162, 78.75) * mm, "end": v(-162, 77.25) * mm});
            skLineSegment(sketch, "E12.direction1", {"start": v(-168, 65.25) * mm, "end": v(-143, 65.25) * mm, "construction": true});
            skLineSegment(sketch, "E12.direction2", {"start": v(-168, 65.25) * mm, "end": v(-168, 77.25) * mm, "construction": true});
            skLineSegment(sketch, "E13.0.0.2", {"start": v(-162, 90.75) * mm, "end": v(-168, 90.75) * mm});
            skLineSegment(sketch, "E13.3.0.2", {"start": v(-162, 89.25) * mm, "end": v(-168, 89.25) * mm});
            skLineSegment(sketch, "E13.6.0.2", {"start": v(-168, 90.75) * mm, "end": v(-168, 89.25) * mm});
            skLineSegment(sketch, "E13.9.0.2", {"start": v(-162, 90.75) * mm, "end": v(-162, 89.25) * mm});
            skLineSegment(sketch, "E13.0.0.3", {"start": v(-162, 102.75) * mm, "end": v(-168, 102.75) * mm});
            skLineSegment(sketch, "E13.3.0.3", {"start": v(-162, 101.25) * mm, "end": v(-168, 101.25) * mm});
            skLineSegment(sketch, "E13.6.0.3", {"start": v(-168, 102.75) * mm, "end": v(-168, 101.25) * mm});
            skLineSegment(sketch, "E13.9.0.3", {"start": v(-162, 102.75) * mm, "end": v(-162, 101.25) * mm});
            skSolve(sketch);
        }
        {
            var Q0;
            {var subQ0=sQuery(id+"F0.wireOp",EDGE,"E3.0.1.16");var subQ1=sQuery(id+"F0.wireOp",EDGE,"6f7ae5fc-1566-4385-bfb5-e6e9eca27b98.0.0.16");var subQ2=sQuery(id+"F0.wireOp",EDGE,"E2.0.8.0");var subQ3=sQuery(id+"F0.wireOp",EDGE,"E2.0.9.0");var subQ4=sQuery(id+"F0.wireOp",EDGE,"E2.0.15.0");var subQ5=sQuery(id+"F0.wireOp",EDGE,"E2.0.14.0");var subQ6=sQuery(id+"F0.wireOp",EDGE,"E2.0.6.0");var subQ7=sQuery(id+"F0.wireOp",EDGE,"E3.0.6.16");var subQ8=sQuery(id+"F0.wireOp",EDGE,"E3.0.9.16");var subQ9=sQuery(id+"F0.wireOp",EDGE,"E2.0.13.0");var subQ10=sQuery(id+"F0.wireOp",EDGE,"E2.0.11.0");var subQ11=sQuery(id+"F0.wireOp",EDGE,"E3.0.14.16");var subQ12=sQuery(id+"F0.wireOp",EDGE,"E2.0.7.0");var subQ13=sQuery(id+"F0.wireOp",EDGE,"E0.right");var subQ14=sQuery(id+"F0.wireOp",EDGE,"E3.0.8.16");var subQ15=sQuery(id+"F0.wireOp",EDGE,"E0.left");var subQ16=sQuery(id+"F0.wireOp",EDGE,"E0.top");var subQ17=sQuery(id+"F0.wireOp",EDGE,"E2.0.4.0");var subQ18=sQuery(id+"F0.wireOp",EDGE,"E2.0.12.0");var subQ19=sQuery(id+"F0.wireOp",EDGE,"E0.bottom");var subQ20=sQuery(id+"F0.wireOp",EDGE,"E1");var subQ21=sQuery(id+"F0.wireOp",EDGE,"E3.0.10.16");var subQ22=sQuery(id+"F0.wireOp",EDGE,"E2.0.1.0");var subQ23=sQuery(id+"F0.wireOp",EDGE,"E2.0.2.0");var subQ24=sQuery(id+"F0.wireOp",EDGE,"E2.0.10.0");var subQ25=sQuery(id+"F0.wireOp",EDGE,"E2.0.3.0");var subQ26=sQuery(id+"F0.wireOp",EDGE,"E3.0.2.16");var subQ27=sQuery(id+"F0.wireOp",EDGE,"E2.0.5.0");var subQ28=sQuery(id+"F0.wireOp",EDGE,"E3.0.3.16");var subQ29=sQuery(id+"F0.wireOp",EDGE,"E3.0.4.16");var subQ30=sQuery(id+"F0.wireOp",EDGE,"E3.0.5.16");var subQ31=sQuery(id+"F0.wireOp",EDGE,"E3.0.7.16");var subQ32=sQuery(id+"F0.wireOp",EDGE,"E3.0.11.16");var subQ33=sQuery(id+"F0.wireOp",EDGE,"E3.0.12.16");var subQ34=sQuery(id+"F0.wireOp",EDGE,"E3.0.13.16");var subQ35=sQuery(id+"F0.wireOp",EDGE,"E3.0.15.16");var subQ36=sQuery(id+"F0.wireOp",EDGE,"E3.0.16.16");Q0=makeQuery(id+"FJqtpdUANZnq3Um_1.boolean.opBoolean","SPLIT",FACE,{"disambiguationData":[TD([makeQuery(id+"F1.opExtrude","SWEPT_FACE",FACE,{"disambiguationData":[OSD([subQ19])]})])],"derivedFrom":makeQuery(id+"F1.opExtrude","CAP_FACE",FACE,{"disambiguationData":[OSD([subQ19,subQ16,subQ15,subQ13,subQ20,subQ22,subQ23,subQ25,subQ17,subQ27,subQ6,subQ12,subQ2,subQ3,subQ24,subQ10,subQ18,subQ9,subQ5,subQ4,subQ1,sQuery(id+"F0.wireOp",EDGE,"E3.0.1.0"),sQuery(id+"F0.wireOp",EDGE,"E3.0.1.1"),sQuery(id+"F0.wireOp",EDGE,"E3.0.1.2"),sQuery(id+"F0.wireOp",EDGE,"E3.0.1.3"),sQuery(id+"F0.wireOp",EDGE,"E3.0.1.4"),sQuery(id+"F0.wireOp",EDGE,"E3.0.1.5"),sQuery(id+"F0.wireOp",EDGE,"E3.0.1.6"),sQuery(id+"F0.wireOp",EDGE,"E3.0.1.7"),sQuery(id+"F0.wireOp",EDGE,"E3.0.1.8"),sQuery(id+"F0.wireOp",EDGE,"E3.0.1.9"),sQuery(id+"F0.wireOp",EDGE,"E3.0.1.10"),sQuery(id+"F0.wireOp",EDGE,"E3.0.1.11"),sQuery(id+"F0.wireOp",EDGE,"E3.0.1.12"),sQuery(id+"F0.wireOp",EDGE,"E3.0.1.13"),sQuery(id+"F0.wireOp",EDGE,"E3.0.1.14"),sQuery(id+"F0.wireOp",EDGE,"E3.0.1.15"),subQ0,sQuery(id+"F0.wireOp",EDGE,"E3.0.2.0"),sQuery(id+"F0.wireOp",EDGE,"E3.0.2.1"),sQuery(id+"F0.wireOp",EDGE,"E3.0.2.2"),sQuery(id+"F0.wireOp",EDGE,"E3.0.2.3"),sQuery(id+"F0.wireOp",EDGE,"E3.0.2.4"),sQuery(id+"F0.wireOp",EDGE,"E3.0.2.5"),sQuery(id+"F0.wireOp",EDGE,"E3.0.2.6"),sQuery(id+"F0.wireOp",EDGE,"E3.0.2.7"),sQuery(id+"F0.wireOp",EDGE,"E3.0.2.8"),sQuery(id+"F0.wireOp",EDGE,"E3.0.2.9"),sQuery(id+"F0.wireOp",EDGE,"E3.0.2.10"),sQuery(id+"F0.wireOp",EDGE,"E3.0.2.11"),sQuery(id+"F0.wireOp",EDGE,"E3.0.2.12"),sQuery(id+"F0.wireOp",EDGE,"E3.0.2.13"),sQuery(id+"F0.wireOp",EDGE,"E3.0.2.14"),sQuery(id+"F0.wireOp",EDGE,"E3.0.2.15"),subQ26,sQuery(id+"F0.wireOp",EDGE,"E3.0.3.0"),sQuery(id+"F0.wireOp",EDGE,"E3.0.3.1"),sQuery(id+"F0.wireOp",EDGE,"E3.0.3.2"),sQuery(id+"F0.wireOp",EDGE,"E3.0.3.3"),sQuery(id+"F0.wireOp",EDGE,"E3.0.3.4"),sQuery(id+"F0.wireOp",EDGE,"E3.0.3.5"),sQuery(id+"F0.wireOp",EDGE,"E3.0.3.6"),sQuery(id+"F0.wireOp",EDGE,"E3.0.3.7"),sQuery(id+"F0.wireOp",EDGE,"E3.0.3.8"),sQuery(id+"F0.wireOp",EDGE,"E3.0.3.9"),sQuery(id+"F0.wireOp",EDGE,"E3.0.3.10"),sQuery(id+"F0.wireOp",EDGE,"E3.0.3.11"),sQuery(id+"F0.wireOp",EDGE,"E3.0.3.12"),sQuery(id+"F0.wireOp",EDGE,"E3.0.3.13"),sQuery(id+"F0.wireOp",EDGE,"E3.0.3.14"),sQuery(id+"F0.wireOp",EDGE,"E3.0.3.15"),subQ28,sQuery(id+"F0.wireOp",EDGE,"E3.0.4.0"),sQuery(id+"F0.wireOp",EDGE,"E3.0.4.1"),sQuery(id+"F0.wireOp",EDGE,"E3.0.4.2"),sQuery(id+"F0.wireOp",EDGE,"E3.0.4.3"),sQuery(id+"F0.wireOp",EDGE,"E3.0.4.4"),sQuery(id+"F0.wireOp",EDGE,"E3.0.4.5"),sQuery(id+"F0.wireOp",EDGE,"E3.0.4.6"),sQuery(id+"F0.wireOp",EDGE,"E3.0.4.7"),sQuery(id+"F0.wireOp",EDGE,"E3.0.4.8"),sQuery(id+"F0.wireOp",EDGE,"E3.0.4.9"),sQuery(id+"F0.wireOp",EDGE,"E3.0.4.10"),sQuery(id+"F0.wireOp",EDGE,"E3.0.4.11"),sQuery(id+"F0.wireOp",EDGE,"E3.0.4.12"),sQuery(id+"F0.wireOp",EDGE,"E3.0.4.13"),sQuery(id+"F0.wireOp",EDGE,"E3.0.4.14"),sQuery(id+"F0.wireOp",EDGE,"E3.0.4.15"),subQ29,sQuery(id+"F0.wireOp",EDGE,"E3.0.5.0"),sQuery(id+"F0.wireOp",EDGE,"E3.0.5.1"),sQuery(id+"F0.wireOp",EDGE,"E3.0.5.2"),sQuery(id+"F0.wireOp",EDGE,"E3.0.5.3"),sQuery(id+"F0.wireOp",EDGE,"E3.0.5.4"),sQuery(id+"F0.wireOp",EDGE,"E3.0.5.5"),sQuery(id+"F0.wireOp",EDGE,"E3.0.5.6"),sQuery(id+"F0.wireOp",EDGE,"E3.0.5.7"),sQuery(id+"F0.wireOp",EDGE,"E3.0.5.8"),sQuery(id+"F0.wireOp",EDGE,"E3.0.5.9"),sQuery(id+"F0.wireOp",EDGE,"E3.0.5.10"),sQuery(id+"F0.wireOp",EDGE,"E3.0.5.11"),sQuery(id+"F0.wireOp",EDGE,"E3.0.5.12"),sQuery(id+"F0.wireOp",EDGE,"E3.0.5.13"),sQuery(id+"F0.wireOp",EDGE,"E3.0.5.14"),sQuery(id+"F0.wireOp",EDGE,"E3.0.5.15"),subQ30,sQuery(id+"F0.wireOp",EDGE,"E3.0.6.0"),sQuery(id+"F0.wireOp",EDGE,"E3.0.6.1"),sQuery(id+"F0.wireOp",EDGE,"E3.0.6.2"),sQuery(id+"F0.wireOp",EDGE,"E3.0.6.3"),sQuery(id+"F0.wireOp",EDGE,"E3.0.6.4"),sQuery(id+"F0.wireOp",EDGE,"E3.0.6.5"),sQuery(id+"F0.wireOp",EDGE,"E3.0.6.6"),sQuery(id+"F0.wireOp",EDGE,"E3.0.6.7"),sQuery(id+"F0.wireOp",EDGE,"E3.0.6.8"),sQuery(id+"F0.wireOp",EDGE,"E3.0.6.9"),sQuery(id+"F0.wireOp",EDGE,"E3.0.6.10"),sQuery(id+"F0.wireOp",EDGE,"E3.0.6.11"),sQuery(id+"F0.wireOp",EDGE,"E3.0.6.12"),sQuery(id+"F0.wireOp",EDGE,"E3.0.6.13"),sQuery(id+"F0.wireOp",EDGE,"E3.0.6.14"),sQuery(id+"F0.wireOp",EDGE,"E3.0.6.15"),subQ7,sQuery(id+"F0.wireOp",EDGE,"E3.0.7.0"),sQuery(id+"F0.wireOp",EDGE,"E3.0.7.1"),sQuery(id+"F0.wireOp",EDGE,"E3.0.7.2"),sQuery(id+"F0.wireOp",EDGE,"E3.0.7.3"),sQuery(id+"F0.wireOp",EDGE,"E3.0.7.4"),sQuery(id+"F0.wireOp",EDGE,"E3.0.7.5"),sQuery(id+"F0.wireOp",EDGE,"E3.0.7.6"),sQuery(id+"F0.wireOp",EDGE,"E3.0.7.7"),sQuery(id+"F0.wireOp",EDGE,"E3.0.7.8"),sQuery(id+"F0.wireOp",EDGE,"E3.0.7.9"),sQuery(id+"F0.wireOp",EDGE,"E3.0.7.10"),sQuery(id+"F0.wireOp",EDGE,"E3.0.7.11"),sQuery(id+"F0.wireOp",EDGE,"E3.0.7.12"),sQuery(id+"F0.wireOp",EDGE,"E3.0.7.13"),sQuery(id+"F0.wireOp",EDGE,"E3.0.7.14"),sQuery(id+"F0.wireOp",EDGE,"E3.0.7.15"),subQ31,sQuery(id+"F0.wireOp",EDGE,"E3.0.8.0"),sQuery(id+"F0.wireOp",EDGE,"E3.0.8.1"),sQuery(id+"F0.wireOp",EDGE,"E3.0.8.2"),sQuery(id+"F0.wireOp",EDGE,"E3.0.8.3"),sQuery(id+"F0.wireOp",EDGE,"E3.0.8.4"),sQuery(id+"F0.wireOp",EDGE,"E3.0.8.5"),sQuery(id+"F0.wireOp",EDGE,"E3.0.8.6"),sQuery(id+"F0.wireOp",EDGE,"E3.0.8.7"),sQuery(id+"F0.wireOp",EDGE,"E3.0.8.8"),sQuery(id+"F0.wireOp",EDGE,"E3.0.8.9"),sQuery(id+"F0.wireOp",EDGE,"E3.0.8.10"),sQuery(id+"F0.wireOp",EDGE,"E3.0.8.11"),sQuery(id+"F0.wireOp",EDGE,"E3.0.8.12"),sQuery(id+"F0.wireOp",EDGE,"E3.0.8.13"),sQuery(id+"F0.wireOp",EDGE,"E3.0.8.14"),sQuery(id+"F0.wireOp",EDGE,"E3.0.8.15"),subQ14,sQuery(id+"F0.wireOp",EDGE,"E3.0.9.0"),sQuery(id+"F0.wireOp",EDGE,"E3.0.9.1"),sQuery(id+"F0.wireOp",EDGE,"E3.0.9.2"),sQuery(id+"F0.wireOp",EDGE,"E3.0.9.3"),sQuery(id+"F0.wireOp",EDGE,"E3.0.9.4"),sQuery(id+"F0.wireOp",EDGE,"E3.0.9.5"),sQuery(id+"F0.wireOp",EDGE,"E3.0.9.6"),sQuery(id+"F0.wireOp",EDGE,"E3.0.9.7"),sQuery(id+"F0.wireOp",EDGE,"E3.0.9.8"),sQuery(id+"F0.wireOp",EDGE,"E3.0.9.9"),sQuery(id+"F0.wireOp",EDGE,"E3.0.9.10"),sQuery(id+"F0.wireOp",EDGE,"E3.0.9.11"),sQuery(id+"F0.wireOp",EDGE,"E3.0.9.12"),sQuery(id+"F0.wireOp",EDGE,"E3.0.9.13"),sQuery(id+"F0.wireOp",EDGE,"E3.0.9.14"),sQuery(id+"F0.wireOp",EDGE,"E3.0.9.15"),subQ8,sQuery(id+"F0.wireOp",EDGE,"E3.0.10.0"),sQuery(id+"F0.wireOp",EDGE,"E3.0.10.1"),sQuery(id+"F0.wireOp",EDGE,"E3.0.10.2"),sQuery(id+"F0.wireOp",EDGE,"E3.0.10.3"),sQuery(id+"F0.wireOp",EDGE,"E3.0.10.4"),sQuery(id+"F0.wireOp",EDGE,"E3.0.10.5"),sQuery(id+"F0.wireOp",EDGE,"E3.0.10.6"),sQuery(id+"F0.wireOp",EDGE,"E3.0.10.7"),sQuery(id+"F0.wireOp",EDGE,"E3.0.10.8"),sQuery(id+"F0.wireOp",EDGE,"E3.0.10.9"),sQuery(id+"F0.wireOp",EDGE,"E3.0.10.10"),sQuery(id+"F0.wireOp",EDGE,"E3.0.10.11"),sQuery(id+"F0.wireOp",EDGE,"E3.0.10.12"),sQuery(id+"F0.wireOp",EDGE,"E3.0.10.13"),sQuery(id+"F0.wireOp",EDGE,"E3.0.10.14"),sQuery(id+"F0.wireOp",EDGE,"E3.0.10.15"),subQ21,sQuery(id+"F0.wireOp",EDGE,"E3.0.11.0"),sQuery(id+"F0.wireOp",EDGE,"E3.0.11.1"),sQuery(id+"F0.wireOp",EDGE,"E3.0.11.2"),sQuery(id+"F0.wireOp",EDGE,"E3.0.11.3"),sQuery(id+"F0.wireOp",EDGE,"E3.0.11.4"),sQuery(id+"F0.wireOp",EDGE,"E3.0.11.5"),sQuery(id+"F0.wireOp",EDGE,"E3.0.11.6"),sQuery(id+"F0.wireOp",EDGE,"E3.0.11.7"),sQuery(id+"F0.wireOp",EDGE,"E3.0.11.8"),sQuery(id+"F0.wireOp",EDGE,"E3.0.11.9"),sQuery(id+"F0.wireOp",EDGE,"E3.0.11.10"),sQuery(id+"F0.wireOp",EDGE,"E3.0.11.11"),sQuery(id+"F0.wireOp",EDGE,"E3.0.11.12"),sQuery(id+"F0.wireOp",EDGE,"E3.0.11.13"),sQuery(id+"F0.wireOp",EDGE,"E3.0.11.14"),sQuery(id+"F0.wireOp",EDGE,"E3.0.11.15"),subQ32,sQuery(id+"F0.wireOp",EDGE,"E3.0.12.0"),sQuery(id+"F0.wireOp",EDGE,"E3.0.12.1"),sQuery(id+"F0.wireOp",EDGE,"E3.0.12.2"),sQuery(id+"F0.wireOp",EDGE,"E3.0.12.3"),sQuery(id+"F0.wireOp",EDGE,"E3.0.12.4"),sQuery(id+"F0.wireOp",EDGE,"E3.0.12.5"),sQuery(id+"F0.wireOp",EDGE,"E3.0.12.6"),sQuery(id+"F0.wireOp",EDGE,"E3.0.12.7"),sQuery(id+"F0.wireOp",EDGE,"E3.0.12.8"),sQuery(id+"F0.wireOp",EDGE,"E3.0.12.9"),sQuery(id+"F0.wireOp",EDGE,"E3.0.12.10"),sQuery(id+"F0.wireOp",EDGE,"E3.0.12.11"),sQuery(id+"F0.wireOp",EDGE,"E3.0.12.12"),sQuery(id+"F0.wireOp",EDGE,"E3.0.12.13"),sQuery(id+"F0.wireOp",EDGE,"E3.0.12.14"),sQuery(id+"F0.wireOp",EDGE,"E3.0.12.15"),subQ33,sQuery(id+"F0.wireOp",EDGE,"E3.0.13.0"),sQuery(id+"F0.wireOp",EDGE,"E3.0.13.1"),sQuery(id+"F0.wireOp",EDGE,"E3.0.13.2"),sQuery(id+"F0.wireOp",EDGE,"E3.0.13.3"),sQuery(id+"F0.wireOp",EDGE,"E3.0.13.4"),sQuery(id+"F0.wireOp",EDGE,"E3.0.13.5"),sQuery(id+"F0.wireOp",EDGE,"E3.0.13.6"),sQuery(id+"F0.wireOp",EDGE,"E3.0.13.7"),sQuery(id+"F0.wireOp",EDGE,"E3.0.13.8"),sQuery(id+"F0.wireOp",EDGE,"E3.0.13.9"),sQuery(id+"F0.wireOp",EDGE,"E3.0.13.10"),sQuery(id+"F0.wireOp",EDGE,"E3.0.13.11"),sQuery(id+"F0.wireOp",EDGE,"E3.0.13.12"),sQuery(id+"F0.wireOp",EDGE,"E3.0.13.13"),sQuery(id+"F0.wireOp",EDGE,"E3.0.13.14"),sQuery(id+"F0.wireOp",EDGE,"E3.0.13.15"),subQ34,sQuery(id+"F0.wireOp",EDGE,"E3.0.14.0"),sQuery(id+"F0.wireOp",EDGE,"E3.0.14.1"),sQuery(id+"F0.wireOp",EDGE,"E3.0.14.2"),sQuery(id+"F0.wireOp",EDGE,"E3.0.14.3"),sQuery(id+"F0.wireOp",EDGE,"E3.0.14.4"),sQuery(id+"F0.wireOp",EDGE,"E3.0.14.5"),sQuery(id+"F0.wireOp",EDGE,"E3.0.14.6"),sQuery(id+"F0.wireOp",EDGE,"E3.0.14.7"),sQuery(id+"F0.wireOp",EDGE,"E3.0.14.8"),sQuery(id+"F0.wireOp",EDGE,"E3.0.14.9"),sQuery(id+"F0.wireOp",EDGE,"E3.0.14.10"),sQuery(id+"F0.wireOp",EDGE,"E3.0.14.11"),sQuery(id+"F0.wireOp",EDGE,"E3.0.14.12"),sQuery(id+"F0.wireOp",EDGE,"E3.0.14.13"),sQuery(id+"F0.wireOp",EDGE,"E3.0.14.14"),sQuery(id+"F0.wireOp",EDGE,"E3.0.14.15"),subQ11,sQuery(id+"F0.wireOp",EDGE,"E3.0.15.0"),sQuery(id+"F0.wireOp",EDGE,"E3.0.15.1"),sQuery(id+"F0.wireOp",EDGE,"E3.0.15.2"),sQuery(id+"F0.wireOp",EDGE,"E3.0.15.3"),sQuery(id+"F0.wireOp",EDGE,"E3.0.15.4"),sQuery(id+"F0.wireOp",EDGE,"E3.0.15.5"),sQuery(id+"F0.wireOp",EDGE,"E3.0.15.6"),sQuery(id+"F0.wireOp",EDGE,"E3.0.15.7"),sQuery(id+"F0.wireOp",EDGE,"E3.0.15.8"),sQuery(id+"F0.wireOp",EDGE,"E3.0.15.9"),sQuery(id+"F0.wireOp",EDGE,"E3.0.15.10"),sQuery(id+"F0.wireOp",EDGE,"E3.0.15.11"),sQuery(id+"F0.wireOp",EDGE,"E3.0.15.12"),sQuery(id+"F0.wireOp",EDGE,"E3.0.15.13"),sQuery(id+"F0.wireOp",EDGE,"E3.0.15.14"),sQuery(id+"F0.wireOp",EDGE,"E3.0.15.15"),subQ35,sQuery(id+"F0.wireOp",EDGE,"E3.0.16.0"),sQuery(id+"F0.wireOp",EDGE,"E3.0.16.1"),sQuery(id+"F0.wireOp",EDGE,"E3.0.16.2"),sQuery(id+"F0.wireOp",EDGE,"E3.0.16.3"),sQuery(id+"F0.wireOp",EDGE,"E3.0.16.4"),sQuery(id+"F0.wireOp",EDGE,"E3.0.16.5"),sQuery(id+"F0.wireOp",EDGE,"E3.0.16.6"),sQuery(id+"F0.wireOp",EDGE,"E3.0.16.7"),sQuery(id+"F0.wireOp",EDGE,"E3.0.16.8"),sQuery(id+"F0.wireOp",EDGE,"E3.0.16.9"),sQuery(id+"F0.wireOp",EDGE,"E3.0.16.10"),sQuery(id+"F0.wireOp",EDGE,"E3.0.16.11"),sQuery(id+"F0.wireOp",EDGE,"E3.0.16.12"),sQuery(id+"F0.wireOp",EDGE,"E3.0.16.13"),sQuery(id+"F0.wireOp",EDGE,"E3.0.16.14"),sQuery(id+"F0.wireOp",EDGE,"E3.0.16.15"),subQ36])],"isStart":false})});}
            var sketch = newSketch(context, id + "F4", { "sketchPlane" : qUnion([Q0])});
            skLineSegment(sketch, "E14.bottom", {"start": v(-102.75, -102) * mm, "end": v(-101.25, -102) * mm});
            skLineSegment(sketch, "E14.top", {"start": v(-102.75, -96.59) * mm, "end": v(-101.25, -96.59) * mm});
            skLineSegment(sketch, "E14.left", {"start": v(-102.75, -96.59) * mm, "end": v(-102.75, -102) * mm});
            skLineSegment(sketch, "E14.right", {"start": v(-101.25, -96.59) * mm, "end": v(-101.25, -102) * mm});
            skLineSegment(sketch, "E15.bottom", {"start": v(-42.75, -102) * mm, "end": v(-41.25, -102) * mm});
            skLineSegment(sketch, "E15.top", {"start": v(-42.75, -99.25) * mm, "end": v(-41.25, -99.25) * mm});
            skLineSegment(sketch, "E15.left", {"start": v(-42.75, -99.25) * mm, "end": v(-42.75, -102) * mm});
            skLineSegment(sketch, "E15.right", {"start": v(-41.25, -99.25) * mm, "end": v(-41.25, -102) * mm});
            skLineSegment(sketch, "E16.bottom", {"start": v(-98.85, -41.25) * mm, "end": v(-162, -41.25) * mm});
            skLineSegment(sketch, "E16.top", {"start": v(-98.85, -42.75) * mm, "end": v(-162, -42.75) * mm});
            skLineSegment(sketch, "E16.left", {"start": v(-98.85, -41.25) * mm, "end": v(-98.85, -42.75) * mm});
            skLineSegment(sketch, "E16.right", {"start": v(-162, -41.25) * mm, "end": v(-162, -42.75) * mm});
            skPoint(sketch, "E17.oppositeSnap0", {"position": v(-84.48, 17.25) * mm});
            skLineSegment(sketch, "E17.bottom", {"start": v(-100.24, 18.75) * mm, "end": v(-162, 18.75) * mm});
            skLineSegment(sketch, "E17.top", {"start": v(-100.24, 17.25) * mm, "end": v(-162, 17.25) * mm});
            skLineSegment(sketch, "E17.left", {"start": v(-162, 18.75) * mm, "end": v(-162, 17.25) * mm});
            skLineSegment(sketch, "E17.right", {"start": v(-100.24, 18.75) * mm, "end": v(-100.24, 17.25) * mm});
            skSolve(sketch);
        }
        {
            var Q0;
            {var subQ0=sQuery(id+"F0.wireOp",EDGE,"E3.0.1.16");var subQ1=sQuery(id+"F0.wireOp",EDGE,"6f7ae5fc-1566-4385-bfb5-e6e9eca27b98.0.0.16");var subQ2=sQuery(id+"F0.wireOp",EDGE,"E2.0.8.0");var subQ3=sQuery(id+"F0.wireOp",EDGE,"E2.0.9.0");var subQ4=sQuery(id+"F0.wireOp",EDGE,"E2.0.15.0");var subQ5=sQuery(id+"F0.wireOp",EDGE,"E2.0.14.0");var subQ6=sQuery(id+"F0.wireOp",EDGE,"E2.0.6.0");var subQ7=sQuery(id+"F0.wireOp",EDGE,"E3.0.6.16");var subQ8=sQuery(id+"F0.wireOp",EDGE,"E3.0.9.16");var subQ9=sQuery(id+"F0.wireOp",EDGE,"E2.0.13.0");var subQ10=sQuery(id+"F0.wireOp",EDGE,"E2.0.11.0");var subQ11=sQuery(id+"F0.wireOp",EDGE,"E3.0.14.16");var subQ12=sQuery(id+"F0.wireOp",EDGE,"E2.0.7.0");var subQ13=sQuery(id+"F0.wireOp",EDGE,"E0.right");var subQ14=sQuery(id+"F0.wireOp",EDGE,"E3.0.8.16");var subQ15=sQuery(id+"F0.wireOp",EDGE,"E0.left");var subQ16=sQuery(id+"F0.wireOp",EDGE,"E0.top");var subQ17=sQuery(id+"F0.wireOp",EDGE,"E2.0.4.0");var subQ18=sQuery(id+"F0.wireOp",EDGE,"E2.0.12.0");var subQ19=sQuery(id+"F0.wireOp",EDGE,"E0.bottom");var subQ20=sQuery(id+"F0.wireOp",EDGE,"E1");var subQ21=sQuery(id+"F0.wireOp",EDGE,"E3.0.10.16");var subQ22=sQuery(id+"F0.wireOp",EDGE,"E2.0.1.0");var subQ23=sQuery(id+"F0.wireOp",EDGE,"E2.0.2.0");var subQ24=sQuery(id+"F0.wireOp",EDGE,"E2.0.10.0");var subQ25=sQuery(id+"F0.wireOp",EDGE,"E2.0.3.0");var subQ26=sQuery(id+"F0.wireOp",EDGE,"E3.0.2.16");var subQ27=sQuery(id+"F0.wireOp",EDGE,"E2.0.5.0");var subQ28=sQuery(id+"F0.wireOp",EDGE,"E3.0.3.16");var subQ29=sQuery(id+"F0.wireOp",EDGE,"E3.0.4.16");var subQ30=sQuery(id+"F0.wireOp",EDGE,"E3.0.5.16");var subQ31=sQuery(id+"F0.wireOp",EDGE,"E3.0.7.16");var subQ32=sQuery(id+"F0.wireOp",EDGE,"E3.0.11.16");var subQ33=sQuery(id+"F0.wireOp",EDGE,"E3.0.12.16");var subQ34=sQuery(id+"F0.wireOp",EDGE,"E3.0.13.16");var subQ35=sQuery(id+"F0.wireOp",EDGE,"E3.0.15.16");var subQ36=sQuery(id+"F0.wireOp",EDGE,"E3.0.16.16");Q0=makeQuery(id+"FJqtpdUANZnq3Um_1.boolean.opBoolean","SPLIT",FACE,{"disambiguationData":[TD([makeQuery(id+"F1.opExtrude","SWEPT_FACE",FACE,{"disambiguationData":[OSD([subQ19])]})])],"derivedFrom":makeQuery(id+"F1.opExtrude","CAP_FACE",FACE,{"disambiguationData":[OSD([subQ19,subQ16,subQ15,subQ13,subQ20,subQ22,subQ23,subQ25,subQ17,subQ27,subQ6,subQ12,subQ2,subQ3,subQ24,subQ10,subQ18,subQ9,subQ5,subQ4,subQ1,sQuery(id+"F0.wireOp",EDGE,"E3.0.1.0"),sQuery(id+"F0.wireOp",EDGE,"E3.0.1.1"),sQuery(id+"F0.wireOp",EDGE,"E3.0.1.2"),sQuery(id+"F0.wireOp",EDGE,"E3.0.1.3"),sQuery(id+"F0.wireOp",EDGE,"E3.0.1.4"),sQuery(id+"F0.wireOp",EDGE,"E3.0.1.5"),sQuery(id+"F0.wireOp",EDGE,"E3.0.1.6"),sQuery(id+"F0.wireOp",EDGE,"E3.0.1.7"),sQuery(id+"F0.wireOp",EDGE,"E3.0.1.8"),sQuery(id+"F0.wireOp",EDGE,"E3.0.1.9"),sQuery(id+"F0.wireOp",EDGE,"E3.0.1.10"),sQuery(id+"F0.wireOp",EDGE,"E3.0.1.11"),sQuery(id+"F0.wireOp",EDGE,"E3.0.1.12"),sQuery(id+"F0.wireOp",EDGE,"E3.0.1.13"),sQuery(id+"F0.wireOp",EDGE,"E3.0.1.14"),sQuery(id+"F0.wireOp",EDGE,"E3.0.1.15"),subQ0,sQuery(id+"F0.wireOp",EDGE,"E3.0.2.0"),sQuery(id+"F0.wireOp",EDGE,"E3.0.2.1"),sQuery(id+"F0.wireOp",EDGE,"E3.0.2.2"),sQuery(id+"F0.wireOp",EDGE,"E3.0.2.3"),sQuery(id+"F0.wireOp",EDGE,"E3.0.2.4"),sQuery(id+"F0.wireOp",EDGE,"E3.0.2.5"),sQuery(id+"F0.wireOp",EDGE,"E3.0.2.6"),sQuery(id+"F0.wireOp",EDGE,"E3.0.2.7"),sQuery(id+"F0.wireOp",EDGE,"E3.0.2.8"),sQuery(id+"F0.wireOp",EDGE,"E3.0.2.9"),sQuery(id+"F0.wireOp",EDGE,"E3.0.2.10"),sQuery(id+"F0.wireOp",EDGE,"E3.0.2.11"),sQuery(id+"F0.wireOp",EDGE,"E3.0.2.12"),sQuery(id+"F0.wireOp",EDGE,"E3.0.2.13"),sQuery(id+"F0.wireOp",EDGE,"E3.0.2.14"),sQuery(id+"F0.wireOp",EDGE,"E3.0.2.15"),subQ26,sQuery(id+"F0.wireOp",EDGE,"E3.0.3.0"),sQuery(id+"F0.wireOp",EDGE,"E3.0.3.1"),sQuery(id+"F0.wireOp",EDGE,"E3.0.3.2"),sQuery(id+"F0.wireOp",EDGE,"E3.0.3.3"),sQuery(id+"F0.wireOp",EDGE,"E3.0.3.4"),sQuery(id+"F0.wireOp",EDGE,"E3.0.3.5"),sQuery(id+"F0.wireOp",EDGE,"E3.0.3.6"),sQuery(id+"F0.wireOp",EDGE,"E3.0.3.7"),sQuery(id+"F0.wireOp",EDGE,"E3.0.3.8"),sQuery(id+"F0.wireOp",EDGE,"E3.0.3.9"),sQuery(id+"F0.wireOp",EDGE,"E3.0.3.10"),sQuery(id+"F0.wireOp",EDGE,"E3.0.3.11"),sQuery(id+"F0.wireOp",EDGE,"E3.0.3.12"),sQuery(id+"F0.wireOp",EDGE,"E3.0.3.13"),sQuery(id+"F0.wireOp",EDGE,"E3.0.3.14"),sQuery(id+"F0.wireOp",EDGE,"E3.0.3.15"),subQ28,sQuery(id+"F0.wireOp",EDGE,"E3.0.4.0"),sQuery(id+"F0.wireOp",EDGE,"E3.0.4.1"),sQuery(id+"F0.wireOp",EDGE,"E3.0.4.2"),sQuery(id+"F0.wireOp",EDGE,"E3.0.4.3"),sQuery(id+"F0.wireOp",EDGE,"E3.0.4.4"),sQuery(id+"F0.wireOp",EDGE,"E3.0.4.5"),sQuery(id+"F0.wireOp",EDGE,"E3.0.4.6"),sQuery(id+"F0.wireOp",EDGE,"E3.0.4.7"),sQuery(id+"F0.wireOp",EDGE,"E3.0.4.8"),sQuery(id+"F0.wireOp",EDGE,"E3.0.4.9"),sQuery(id+"F0.wireOp",EDGE,"E3.0.4.10"),sQuery(id+"F0.wireOp",EDGE,"E3.0.4.11"),sQuery(id+"F0.wireOp",EDGE,"E3.0.4.12"),sQuery(id+"F0.wireOp",EDGE,"E3.0.4.13"),sQuery(id+"F0.wireOp",EDGE,"E3.0.4.14"),sQuery(id+"F0.wireOp",EDGE,"E3.0.4.15"),subQ29,sQuery(id+"F0.wireOp",EDGE,"E3.0.5.0"),sQuery(id+"F0.wireOp",EDGE,"E3.0.5.1"),sQuery(id+"F0.wireOp",EDGE,"E3.0.5.2"),sQuery(id+"F0.wireOp",EDGE,"E3.0.5.3"),sQuery(id+"F0.wireOp",EDGE,"E3.0.5.4"),sQuery(id+"F0.wireOp",EDGE,"E3.0.5.5"),sQuery(id+"F0.wireOp",EDGE,"E3.0.5.6"),sQuery(id+"F0.wireOp",EDGE,"E3.0.5.7"),sQuery(id+"F0.wireOp",EDGE,"E3.0.5.8"),sQuery(id+"F0.wireOp",EDGE,"E3.0.5.9"),sQuery(id+"F0.wireOp",EDGE,"E3.0.5.10"),sQuery(id+"F0.wireOp",EDGE,"E3.0.5.11"),sQuery(id+"F0.wireOp",EDGE,"E3.0.5.12"),sQuery(id+"F0.wireOp",EDGE,"E3.0.5.13"),sQuery(id+"F0.wireOp",EDGE,"E3.0.5.14"),sQuery(id+"F0.wireOp",EDGE,"E3.0.5.15"),subQ30,sQuery(id+"F0.wireOp",EDGE,"E3.0.6.0"),sQuery(id+"F0.wireOp",EDGE,"E3.0.6.1"),sQuery(id+"F0.wireOp",EDGE,"E3.0.6.2"),sQuery(id+"F0.wireOp",EDGE,"E3.0.6.3"),sQuery(id+"F0.wireOp",EDGE,"E3.0.6.4"),sQuery(id+"F0.wireOp",EDGE,"E3.0.6.5"),sQuery(id+"F0.wireOp",EDGE,"E3.0.6.6"),sQuery(id+"F0.wireOp",EDGE,"E3.0.6.7"),sQuery(id+"F0.wireOp",EDGE,"E3.0.6.8"),sQuery(id+"F0.wireOp",EDGE,"E3.0.6.9"),sQuery(id+"F0.wireOp",EDGE,"E3.0.6.10"),sQuery(id+"F0.wireOp",EDGE,"E3.0.6.11"),sQuery(id+"F0.wireOp",EDGE,"E3.0.6.12"),sQuery(id+"F0.wireOp",EDGE,"E3.0.6.13"),sQuery(id+"F0.wireOp",EDGE,"E3.0.6.14"),sQuery(id+"F0.wireOp",EDGE,"E3.0.6.15"),subQ7,sQuery(id+"F0.wireOp",EDGE,"E3.0.7.0"),sQuery(id+"F0.wireOp",EDGE,"E3.0.7.1"),sQuery(id+"F0.wireOp",EDGE,"E3.0.7.2"),sQuery(id+"F0.wireOp",EDGE,"E3.0.7.3"),sQuery(id+"F0.wireOp",EDGE,"E3.0.7.4"),sQuery(id+"F0.wireOp",EDGE,"E3.0.7.5"),sQuery(id+"F0.wireOp",EDGE,"E3.0.7.6"),sQuery(id+"F0.wireOp",EDGE,"E3.0.7.7"),sQuery(id+"F0.wireOp",EDGE,"E3.0.7.8"),sQuery(id+"F0.wireOp",EDGE,"E3.0.7.9"),sQuery(id+"F0.wireOp",EDGE,"E3.0.7.10"),sQuery(id+"F0.wireOp",EDGE,"E3.0.7.11"),sQuery(id+"F0.wireOp",EDGE,"E3.0.7.12"),sQuery(id+"F0.wireOp",EDGE,"E3.0.7.13"),sQuery(id+"F0.wireOp",EDGE,"E3.0.7.14"),sQuery(id+"F0.wireOp",EDGE,"E3.0.7.15"),subQ31,sQuery(id+"F0.wireOp",EDGE,"E3.0.8.0"),sQuery(id+"F0.wireOp",EDGE,"E3.0.8.1"),sQuery(id+"F0.wireOp",EDGE,"E3.0.8.2"),sQuery(id+"F0.wireOp",EDGE,"E3.0.8.3"),sQuery(id+"F0.wireOp",EDGE,"E3.0.8.4"),sQuery(id+"F0.wireOp",EDGE,"E3.0.8.5"),sQuery(id+"F0.wireOp",EDGE,"E3.0.8.6"),sQuery(id+"F0.wireOp",EDGE,"E3.0.8.7"),sQuery(id+"F0.wireOp",EDGE,"E3.0.8.8"),sQuery(id+"F0.wireOp",EDGE,"E3.0.8.9"),sQuery(id+"F0.wireOp",EDGE,"E3.0.8.10"),sQuery(id+"F0.wireOp",EDGE,"E3.0.8.11"),sQuery(id+"F0.wireOp",EDGE,"E3.0.8.12"),sQuery(id+"F0.wireOp",EDGE,"E3.0.8.13"),sQuery(id+"F0.wireOp",EDGE,"E3.0.8.14"),sQuery(id+"F0.wireOp",EDGE,"E3.0.8.15"),subQ14,sQuery(id+"F0.wireOp",EDGE,"E3.0.9.0"),sQuery(id+"F0.wireOp",EDGE,"E3.0.9.1"),sQuery(id+"F0.wireOp",EDGE,"E3.0.9.2"),sQuery(id+"F0.wireOp",EDGE,"E3.0.9.3"),sQuery(id+"F0.wireOp",EDGE,"E3.0.9.4"),sQuery(id+"F0.wireOp",EDGE,"E3.0.9.5"),sQuery(id+"F0.wireOp",EDGE,"E3.0.9.6"),sQuery(id+"F0.wireOp",EDGE,"E3.0.9.7"),sQuery(id+"F0.wireOp",EDGE,"E3.0.9.8"),sQuery(id+"F0.wireOp",EDGE,"E3.0.9.9"),sQuery(id+"F0.wireOp",EDGE,"E3.0.9.10"),sQuery(id+"F0.wireOp",EDGE,"E3.0.9.11"),sQuery(id+"F0.wireOp",EDGE,"E3.0.9.12"),sQuery(id+"F0.wireOp",EDGE,"E3.0.9.13"),sQuery(id+"F0.wireOp",EDGE,"E3.0.9.14"),sQuery(id+"F0.wireOp",EDGE,"E3.0.9.15"),subQ8,sQuery(id+"F0.wireOp",EDGE,"E3.0.10.0"),sQuery(id+"F0.wireOp",EDGE,"E3.0.10.1"),sQuery(id+"F0.wireOp",EDGE,"E3.0.10.2"),sQuery(id+"F0.wireOp",EDGE,"E3.0.10.3"),sQuery(id+"F0.wireOp",EDGE,"E3.0.10.4"),sQuery(id+"F0.wireOp",EDGE,"E3.0.10.5"),sQuery(id+"F0.wireOp",EDGE,"E3.0.10.6"),sQuery(id+"F0.wireOp",EDGE,"E3.0.10.7"),sQuery(id+"F0.wireOp",EDGE,"E3.0.10.8"),sQuery(id+"F0.wireOp",EDGE,"E3.0.10.9"),sQuery(id+"F0.wireOp",EDGE,"E3.0.10.10"),sQuery(id+"F0.wireOp",EDGE,"E3.0.10.11"),sQuery(id+"F0.wireOp",EDGE,"E3.0.10.12"),sQuery(id+"F0.wireOp",EDGE,"E3.0.10.13"),sQuery(id+"F0.wireOp",EDGE,"E3.0.10.14"),sQuery(id+"F0.wireOp",EDGE,"E3.0.10.15"),subQ21,sQuery(id+"F0.wireOp",EDGE,"E3.0.11.0"),sQuery(id+"F0.wireOp",EDGE,"E3.0.11.1"),sQuery(id+"F0.wireOp",EDGE,"E3.0.11.2"),sQuery(id+"F0.wireOp",EDGE,"E3.0.11.3"),sQuery(id+"F0.wireOp",EDGE,"E3.0.11.4"),sQuery(id+"F0.wireOp",EDGE,"E3.0.11.5"),sQuery(id+"F0.wireOp",EDGE,"E3.0.11.6"),sQuery(id+"F0.wireOp",EDGE,"E3.0.11.7"),sQuery(id+"F0.wireOp",EDGE,"E3.0.11.8"),sQuery(id+"F0.wireOp",EDGE,"E3.0.11.9"),sQuery(id+"F0.wireOp",EDGE,"E3.0.11.10"),sQuery(id+"F0.wireOp",EDGE,"E3.0.11.11"),sQuery(id+"F0.wireOp",EDGE,"E3.0.11.12"),sQuery(id+"F0.wireOp",EDGE,"E3.0.11.13"),sQuery(id+"F0.wireOp",EDGE,"E3.0.11.14"),sQuery(id+"F0.wireOp",EDGE,"E3.0.11.15"),subQ32,sQuery(id+"F0.wireOp",EDGE,"E3.0.12.0"),sQuery(id+"F0.wireOp",EDGE,"E3.0.12.1"),sQuery(id+"F0.wireOp",EDGE,"E3.0.12.2"),sQuery(id+"F0.wireOp",EDGE,"E3.0.12.3"),sQuery(id+"F0.wireOp",EDGE,"E3.0.12.4"),sQuery(id+"F0.wireOp",EDGE,"E3.0.12.5"),sQuery(id+"F0.wireOp",EDGE,"E3.0.12.6"),sQuery(id+"F0.wireOp",EDGE,"E3.0.12.7"),sQuery(id+"F0.wireOp",EDGE,"E3.0.12.8"),sQuery(id+"F0.wireOp",EDGE,"E3.0.12.9"),sQuery(id+"F0.wireOp",EDGE,"E3.0.12.10"),sQuery(id+"F0.wireOp",EDGE,"E3.0.12.11"),sQuery(id+"F0.wireOp",EDGE,"E3.0.12.12"),sQuery(id+"F0.wireOp",EDGE,"E3.0.12.13"),sQuery(id+"F0.wireOp",EDGE,"E3.0.12.14"),sQuery(id+"F0.wireOp",EDGE,"E3.0.12.15"),subQ33,sQuery(id+"F0.wireOp",EDGE,"E3.0.13.0"),sQuery(id+"F0.wireOp",EDGE,"E3.0.13.1"),sQuery(id+"F0.wireOp",EDGE,"E3.0.13.2"),sQuery(id+"F0.wireOp",EDGE,"E3.0.13.3"),sQuery(id+"F0.wireOp",EDGE,"E3.0.13.4"),sQuery(id+"F0.wireOp",EDGE,"E3.0.13.5"),sQuery(id+"F0.wireOp",EDGE,"E3.0.13.6"),sQuery(id+"F0.wireOp",EDGE,"E3.0.13.7"),sQuery(id+"F0.wireOp",EDGE,"E3.0.13.8"),sQuery(id+"F0.wireOp",EDGE,"E3.0.13.9"),sQuery(id+"F0.wireOp",EDGE,"E3.0.13.10"),sQuery(id+"F0.wireOp",EDGE,"E3.0.13.11"),sQuery(id+"F0.wireOp",EDGE,"E3.0.13.12"),sQuery(id+"F0.wireOp",EDGE,"E3.0.13.13"),sQuery(id+"F0.wireOp",EDGE,"E3.0.13.14"),sQuery(id+"F0.wireOp",EDGE,"E3.0.13.15"),subQ34,sQuery(id+"F0.wireOp",EDGE,"E3.0.14.0"),sQuery(id+"F0.wireOp",EDGE,"E3.0.14.1"),sQuery(id+"F0.wireOp",EDGE,"E3.0.14.2"),sQuery(id+"F0.wireOp",EDGE,"E3.0.14.3"),sQuery(id+"F0.wireOp",EDGE,"E3.0.14.4"),sQuery(id+"F0.wireOp",EDGE,"E3.0.14.5"),sQuery(id+"F0.wireOp",EDGE,"E3.0.14.6"),sQuery(id+"F0.wireOp",EDGE,"E3.0.14.7"),sQuery(id+"F0.wireOp",EDGE,"E3.0.14.8"),sQuery(id+"F0.wireOp",EDGE,"E3.0.14.9"),sQuery(id+"F0.wireOp",EDGE,"E3.0.14.10"),sQuery(id+"F0.wireOp",EDGE,"E3.0.14.11"),sQuery(id+"F0.wireOp",EDGE,"E3.0.14.12"),sQuery(id+"F0.wireOp",EDGE,"E3.0.14.13"),sQuery(id+"F0.wireOp",EDGE,"E3.0.14.14"),sQuery(id+"F0.wireOp",EDGE,"E3.0.14.15"),subQ11,sQuery(id+"F0.wireOp",EDGE,"E3.0.15.0"),sQuery(id+"F0.wireOp",EDGE,"E3.0.15.1"),sQuery(id+"F0.wireOp",EDGE,"E3.0.15.2"),sQuery(id+"F0.wireOp",EDGE,"E3.0.15.3"),sQuery(id+"F0.wireOp",EDGE,"E3.0.15.4"),sQuery(id+"F0.wireOp",EDGE,"E3.0.15.5"),sQuery(id+"F0.wireOp",EDGE,"E3.0.15.6"),sQuery(id+"F0.wireOp",EDGE,"E3.0.15.7"),sQuery(id+"F0.wireOp",EDGE,"E3.0.15.8"),sQuery(id+"F0.wireOp",EDGE,"E3.0.15.9"),sQuery(id+"F0.wireOp",EDGE,"E3.0.15.10"),sQuery(id+"F0.wireOp",EDGE,"E3.0.15.11"),sQuery(id+"F0.wireOp",EDGE,"E3.0.15.12"),sQuery(id+"F0.wireOp",EDGE,"E3.0.15.13"),sQuery(id+"F0.wireOp",EDGE,"E3.0.15.14"),sQuery(id+"F0.wireOp",EDGE,"E3.0.15.15"),subQ35,sQuery(id+"F0.wireOp",EDGE,"E3.0.16.0"),sQuery(id+"F0.wireOp",EDGE,"E3.0.16.1"),sQuery(id+"F0.wireOp",EDGE,"E3.0.16.2"),sQuery(id+"F0.wireOp",EDGE,"E3.0.16.3"),sQuery(id+"F0.wireOp",EDGE,"E3.0.16.4"),sQuery(id+"F0.wireOp",EDGE,"E3.0.16.5"),sQuery(id+"F0.wireOp",EDGE,"E3.0.16.6"),sQuery(id+"F0.wireOp",EDGE,"E3.0.16.7"),sQuery(id+"F0.wireOp",EDGE,"E3.0.16.8"),sQuery(id+"F0.wireOp",EDGE,"E3.0.16.9"),sQuery(id+"F0.wireOp",EDGE,"E3.0.16.10"),sQuery(id+"F0.wireOp",EDGE,"E3.0.16.11"),sQuery(id+"F0.wireOp",EDGE,"E3.0.16.12"),sQuery(id+"F0.wireOp",EDGE,"E3.0.16.13"),sQuery(id+"F0.wireOp",EDGE,"E3.0.16.14"),sQuery(id+"F0.wireOp",EDGE,"E3.0.16.15"),subQ36])],"isStart":false})});}
            var sketch = newSketch(context, id + "F5", { "sketchPlane" : qUnion([Q0])});
            skPoint(sketch, "E18.orphan", {"position": v(0, 114) * mm});
            skPoint(sketch, "E19.startSnap0", {"position": v(91.88, -83.75) * mm});
            skPoint(sketch, "E20.orphan", {"position": v(174, 0) * mm});
            skLineSegment(sketch, "E21.bottom", {"start": v(-174, -114) * mm, "end": v(174, -114) * mm});
            skLineSegment(sketch, "E21.top", {"start": v(-174, 114) * mm, "end": v(174, 114) * mm});
            skLineSegment(sketch, "E21.left", {"start": v(-174, -114) * mm, "end": v(-174, 114) * mm});
            skLineSegment(sketch, "E21.right", {"start": v(174, -114) * mm, "end": v(174, 114) * mm});
            skSolve(sketch);
        }
        {
            var Q0;
            Q0=qSketchRegion(id+"F5",true);
            extrude(context, id + "F6", {"entities" : qUnion([Q0]), "operationType" : NewBodyOperationType.INTERSECT, "oppositeDirection" : true, "depth" : 25 * mm});
        }
        {
            var Q0;
            {var subQ0=sQuery(id+"F0.wireOp",EDGE,"E3.0.13.0");var subQ1=sQuery(id+"F0.wireOp",EDGE,"E3.0.12.14");var subQ2=sQuery(id+"F0.wireOp",EDGE,"E3.0.12.13");var subQ3=sQuery(id+"F0.wireOp",EDGE,"E3.0.12.12");var subQ4=sQuery(id+"F0.wireOp",EDGE,"E3.0.12.11");var subQ5=sQuery(id+"F0.wireOp",EDGE,"E3.0.12.10");var subQ6=sQuery(id+"F0.wireOp",EDGE,"E3.0.12.9");var subQ7=sQuery(id+"F0.wireOp",EDGE,"E3.0.12.8");var subQ8=sQuery(id+"F0.wireOp",EDGE,"E3.0.12.7");var subQ9=sQuery(id+"F0.wireOp",EDGE,"E3.0.12.6");var subQ10=sQuery(id+"F0.wireOp",EDGE,"E3.0.12.5");var subQ11=sQuery(id+"F0.wireOp",EDGE,"E3.0.12.4");var subQ12=sQuery(id+"F0.wireOp",EDGE,"E3.0.12.3");var subQ13=sQuery(id+"F0.wireOp",EDGE,"E3.0.12.2");var subQ14=sQuery(id+"F0.wireOp",EDGE,"E3.0.12.1");var subQ15=sQuery(id+"F0.wireOp",EDGE,"E3.0.12.0");var subQ16=sQuery(id+"F0.wireOp",EDGE,"E3.0.11.14");var subQ17=sQuery(id+"F0.wireOp",EDGE,"E3.0.11.13");var subQ18=sQuery(id+"F0.wireOp",EDGE,"E3.0.11.12");var subQ19=sQuery(id+"F0.wireOp",EDGE,"E3.0.11.11");var subQ20=sQuery(id+"F0.wireOp",EDGE,"E3.0.11.10");var subQ21=sQuery(id+"F0.wireOp",EDGE,"E3.0.11.9");var subQ22=sQuery(id+"F0.wireOp",EDGE,"E3.0.11.8");var subQ23=sQuery(id+"F0.wireOp",EDGE,"E3.0.11.7");var subQ24=sQuery(id+"F0.wireOp",EDGE,"E3.0.11.6");var subQ25=sQuery(id+"F0.wireOp",EDGE,"E3.0.11.5");var subQ26=sQuery(id+"F0.wireOp",EDGE,"E3.0.11.4");var subQ27=sQuery(id+"F0.wireOp",EDGE,"E3.0.11.3");var subQ28=sQuery(id+"F0.wireOp",EDGE,"E3.0.11.2");var subQ29=sQuery(id+"F0.wireOp",EDGE,"E3.0.11.1");var subQ30=sQuery(id+"F0.wireOp",EDGE,"E3.0.11.0");var subQ31=sQuery(id+"F0.wireOp",EDGE,"E3.0.10.14");var subQ32=sQuery(id+"F0.wireOp",EDGE,"E3.0.10.13");var subQ33=sQuery(id+"F0.wireOp",EDGE,"E3.0.10.12");var subQ34=sQuery(id+"F0.wireOp",EDGE,"E3.0.10.11");var subQ35=sQuery(id+"F0.wireOp",EDGE,"E3.0.10.10");var subQ36=sQuery(id+"F0.wireOp",EDGE,"E3.0.10.9");var subQ37=sQuery(id+"F0.wireOp",EDGE,"E3.0.10.8");var subQ38=sQuery(id+"F0.wireOp",EDGE,"E3.0.10.7");var subQ39=sQuery(id+"F0.wireOp",EDGE,"E3.0.10.6");var subQ40=sQuery(id+"F0.wireOp",EDGE,"E3.0.10.5");var subQ41=sQuery(id+"F0.wireOp",EDGE,"E3.0.10.4");var subQ42=sQuery(id+"F0.wireOp",EDGE,"E3.0.10.3");var subQ43=sQuery(id+"F0.wireOp",EDGE,"E3.0.10.2");var subQ44=sQuery(id+"F0.wireOp",EDGE,"E3.0.10.1");var subQ45=sQuery(id+"F0.wireOp",EDGE,"E3.0.10.0");var subQ46=sQuery(id+"F0.wireOp",EDGE,"E3.0.9.14");var subQ47=sQuery(id+"F0.wireOp",EDGE,"E3.0.9.13");var subQ48=sQuery(id+"F0.wireOp",EDGE,"E3.0.9.12");var subQ49=sQuery(id+"F0.wireOp",EDGE,"E3.0.9.11");var subQ50=sQuery(id+"F0.wireOp",EDGE,"E3.0.9.10");var subQ51=sQuery(id+"F0.wireOp",EDGE,"E3.0.9.9");var subQ52=sQuery(id+"F0.wireOp",EDGE,"E3.0.9.8");var subQ53=sQuery(id+"F0.wireOp",EDGE,"E3.0.9.7");var subQ54=sQuery(id+"F0.wireOp",EDGE,"E3.0.9.6");var subQ55=sQuery(id+"F0.wireOp",EDGE,"E3.0.9.5");var subQ56=sQuery(id+"F0.wireOp",EDGE,"E3.0.9.4");var subQ57=sQuery(id+"F0.wireOp",EDGE,"E3.0.9.3");var subQ58=sQuery(id+"F0.wireOp",EDGE,"E3.0.9.2");var subQ59=sQuery(id+"F0.wireOp",EDGE,"E3.0.9.1");var subQ60=sQuery(id+"F0.wireOp",EDGE,"E3.0.9.0");var subQ61=sQuery(id+"F0.wireOp",EDGE,"E3.0.8.14");var subQ62=sQuery(id+"F0.wireOp",EDGE,"E3.0.8.13");var subQ63=sQuery(id+"F0.wireOp",EDGE,"E3.0.8.12");var subQ64=sQuery(id+"F0.wireOp",EDGE,"E3.0.8.11");var subQ65=sQuery(id+"F0.wireOp",EDGE,"E3.0.8.10");var subQ66=sQuery(id+"F0.wireOp",EDGE,"E3.0.8.9");var subQ67=sQuery(id+"F0.wireOp",EDGE,"E3.0.8.8");var subQ68=sQuery(id+"F0.wireOp",EDGE,"E3.0.8.7");var subQ69=sQuery(id+"F0.wireOp",EDGE,"E3.0.8.6");var subQ70=sQuery(id+"F0.wireOp",EDGE,"E3.0.8.5");var subQ71=sQuery(id+"F0.wireOp",EDGE,"E3.0.8.4");var subQ72=sQuery(id+"F0.wireOp",EDGE,"E3.0.8.3");var subQ73=sQuery(id+"F0.wireOp",EDGE,"E3.0.8.2");var subQ74=sQuery(id+"F0.wireOp",EDGE,"E3.0.8.1");var subQ75=sQuery(id+"F0.wireOp",EDGE,"E3.0.8.0");var subQ76=sQuery(id+"F0.wireOp",EDGE,"E3.0.7.14");var subQ77=sQuery(id+"F0.wireOp",EDGE,"E3.0.7.13");var subQ78=sQuery(id+"F0.wireOp",EDGE,"E3.0.7.12");var subQ79=sQuery(id+"F0.wireOp",EDGE,"E3.0.7.11");var subQ80=sQuery(id+"F0.wireOp",EDGE,"E3.0.7.10");var subQ81=sQuery(id+"F0.wireOp",EDGE,"E3.0.7.9");var subQ82=sQuery(id+"F0.wireOp",EDGE,"E3.0.7.8");var subQ83=sQuery(id+"F0.wireOp",EDGE,"E3.0.7.7");var subQ84=sQuery(id+"F0.wireOp",EDGE,"E3.0.7.6");var subQ85=sQuery(id+"F0.wireOp",EDGE,"E3.0.7.5");var subQ86=sQuery(id+"F0.wireOp",EDGE,"E3.0.7.4");var subQ87=sQuery(id+"F0.wireOp",EDGE,"E3.0.7.3");var subQ88=sQuery(id+"F0.wireOp",EDGE,"E3.0.7.2");var subQ89=sQuery(id+"F0.wireOp",EDGE,"E3.0.7.1");var subQ90=sQuery(id+"F0.wireOp",EDGE,"E3.0.7.0");var subQ91=sQuery(id+"F0.wireOp",EDGE,"E3.0.6.14");var subQ92=sQuery(id+"F0.wireOp",EDGE,"E3.0.6.13");var subQ93=sQuery(id+"F0.wireOp",EDGE,"E3.0.6.12");var subQ94=sQuery(id+"F0.wireOp",EDGE,"E3.0.6.11");var subQ95=sQuery(id+"F0.wireOp",EDGE,"E3.0.6.10");var subQ96=sQuery(id+"F0.wireOp",EDGE,"E3.0.6.9");var subQ97=sQuery(id+"F0.wireOp",EDGE,"E3.0.6.8");var subQ98=sQuery(id+"F0.wireOp",EDGE,"E3.0.6.7");var subQ99=sQuery(id+"F0.wireOp",EDGE,"E3.0.6.6");var subQ100=sQuery(id+"F0.wireOp",EDGE,"E3.0.6.5");var subQ101=sQuery(id+"F0.wireOp",EDGE,"E3.0.2.13");var subQ102=sQuery(id+"F0.wireOp",EDGE,"E3.0.2.12");var subQ103=sQuery(id+"F0.wireOp",EDGE,"E3.0.2.11");var subQ104=sQuery(id+"F0.wireOp",EDGE,"E3.0.2.10");var subQ105=sQuery(id+"F0.wireOp",EDGE,"E3.0.2.9");var subQ106=sQuery(id+"F0.wireOp",EDGE,"E3.0.2.8");var subQ107=sQuery(id+"F0.wireOp",EDGE,"E3.0.2.7");var subQ108=sQuery(id+"F0.wireOp",EDGE,"E3.0.2.6");var subQ109=sQuery(id+"F0.wireOp",EDGE,"E3.0.2.5");var subQ110=sQuery(id+"F0.wireOp",EDGE,"E3.0.2.4");var subQ111=sQuery(id+"F0.wireOp",EDGE,"E3.0.2.3");var subQ112=sQuery(id+"F0.wireOp",EDGE,"E3.0.2.2");var subQ113=sQuery(id+"F0.wireOp",EDGE,"E3.0.2.1");var subQ114=sQuery(id+"F0.wireOp",EDGE,"E3.0.2.0");var subQ115=sQuery(id+"F0.wireOp",EDGE,"E3.0.1.14");var subQ116=sQuery(id+"F0.wireOp",EDGE,"E3.0.1.13");var subQ117=sQuery(id+"F0.wireOp",EDGE,"E3.0.1.12");var subQ118=sQuery(id+"F0.wireOp",EDGE,"E3.0.1.11");var subQ119=sQuery(id+"F0.wireOp",EDGE,"E3.0.1.10");var subQ120=sQuery(id+"F0.wireOp",EDGE,"E3.0.1.9");var subQ121=sQuery(id+"F0.wireOp",EDGE,"E3.0.1.8");var subQ122=sQuery(id+"F0.wireOp",EDGE,"E3.0.1.7");var subQ123=sQuery(id+"F0.wireOp",EDGE,"E3.0.1.6");var subQ124=sQuery(id+"F0.wireOp",EDGE,"E2.0.7.0");var subQ125=sQuery(id+"F0.wireOp",EDGE,"E2.0.6.0");var subQ126=sQuery(id+"F0.wireOp",EDGE,"E2.0.5.0");var subQ127=sQuery(id+"F0.wireOp",EDGE,"E2.0.4.0");var subQ128=sQuery(id+"F0.wireOp",EDGE,"E2.0.3.0");var subQ129=sQuery(id+"F0.wireOp",EDGE,"E2.0.2.0");var subQ130=sQuery(id+"F0.wireOp",EDGE,"E3.0.2.14");var subQ131=sQuery(id+"F0.wireOp",EDGE,"E3.0.13.1");var subQ132=sQuery(id+"F0.wireOp",EDGE,"E0.top");var subQ133=sQuery(id+"F0.wireOp",EDGE,"E3.0.6.4");var subQ134=sQuery(id+"F0.wireOp",EDGE,"E3.0.1.5");var subQ135=sQuery(id+"F0.wireOp",EDGE,"E0.right");var subQ136=sQuery(id+"F0.wireOp",EDGE,"E1");var subQ137=sQuery(id+"F0.wireOp",EDGE,"E2.0.1.0");var subQ138=sQuery(id+"F0.wireOp",EDGE,"E2.0.8.0");var subQ139=sQuery(id+"F0.wireOp",EDGE,"E2.0.9.0");var subQ140=sQuery(id+"F0.wireOp",EDGE,"E2.0.10.0");var subQ141=sQuery(id+"F0.wireOp",EDGE,"E2.0.11.0");var subQ142=sQuery(id+"F0.wireOp",EDGE,"E2.0.12.0");var subQ143=sQuery(id+"F0.wireOp",EDGE,"E2.0.13.0");var subQ144=sQuery(id+"F0.wireOp",EDGE,"E3.0.1.0");var subQ145=sQuery(id+"F0.wireOp",EDGE,"E3.0.1.1");var subQ146=sQuery(id+"F0.wireOp",EDGE,"E3.0.1.2");var subQ147=sQuery(id+"F0.wireOp",EDGE,"E3.0.1.3");var subQ148=sQuery(id+"F0.wireOp",EDGE,"E3.0.1.4");var subQ149=sQuery(id+"F0.wireOp",EDGE,"E3.0.3.0");var subQ150=sQuery(id+"F0.wireOp",EDGE,"E3.0.3.1");var subQ151=sQuery(id+"F0.wireOp",EDGE,"E3.0.3.2");var subQ152=sQuery(id+"F0.wireOp",EDGE,"E3.0.3.3");var subQ153=sQuery(id+"F0.wireOp",EDGE,"E3.0.3.4");var subQ154=sQuery(id+"F0.wireOp",EDGE,"E3.0.3.5");var subQ155=sQuery(id+"F0.wireOp",EDGE,"E3.0.3.6");var subQ156=sQuery(id+"F0.wireOp",EDGE,"E3.0.3.7");var subQ157=sQuery(id+"F0.wireOp",EDGE,"E3.0.3.8");var subQ158=sQuery(id+"F0.wireOp",EDGE,"E3.0.3.9");var subQ159=sQuery(id+"F0.wireOp",EDGE,"E3.0.3.10");var subQ160=sQuery(id+"F0.wireOp",EDGE,"E3.0.3.11");var subQ161=sQuery(id+"F0.wireOp",EDGE,"E3.0.3.12");var subQ162=sQuery(id+"F0.wireOp",EDGE,"E3.0.3.13");var subQ163=sQuery(id+"F0.wireOp",EDGE,"E3.0.3.14");var subQ164=sQuery(id+"F0.wireOp",EDGE,"E3.0.4.0");var subQ165=sQuery(id+"F0.wireOp",EDGE,"E3.0.4.1");var subQ166=sQuery(id+"F0.wireOp",EDGE,"E3.0.4.2");var subQ167=sQuery(id+"F0.wireOp",EDGE,"E3.0.4.3");var subQ168=sQuery(id+"F0.wireOp",EDGE,"E3.0.4.4");var subQ169=sQuery(id+"F0.wireOp",EDGE,"E3.0.4.5");var subQ170=sQuery(id+"F0.wireOp",EDGE,"E3.0.4.6");var subQ171=sQuery(id+"F0.wireOp",EDGE,"E3.0.4.7");var subQ172=sQuery(id+"F0.wireOp",EDGE,"E3.0.4.8");var subQ173=sQuery(id+"F0.wireOp",EDGE,"E3.0.4.9");var subQ174=sQuery(id+"F0.wireOp",EDGE,"E3.0.4.10");var subQ175=sQuery(id+"F0.wireOp",EDGE,"E3.0.4.11");var subQ176=sQuery(id+"F0.wireOp",EDGE,"E3.0.4.12");var subQ177=sQuery(id+"F0.wireOp",EDGE,"E3.0.4.13");var subQ178=sQuery(id+"F0.wireOp",EDGE,"E3.0.4.14");var subQ179=sQuery(id+"F0.wireOp",EDGE,"E3.0.5.0");var subQ180=sQuery(id+"F0.wireOp",EDGE,"E3.0.5.1");var subQ181=sQuery(id+"F0.wireOp",EDGE,"E3.0.5.2");var subQ182=sQuery(id+"F0.wireOp",EDGE,"E3.0.5.3");var subQ183=sQuery(id+"F0.wireOp",EDGE,"E3.0.5.4");var subQ184=sQuery(id+"F0.wireOp",EDGE,"E3.0.5.5");var subQ185=sQuery(id+"F0.wireOp",EDGE,"E3.0.5.6");var subQ186=sQuery(id+"F0.wireOp",EDGE,"E3.0.5.7");var subQ187=sQuery(id+"F0.wireOp",EDGE,"E3.0.5.8");var subQ188=sQuery(id+"F0.wireOp",EDGE,"E3.0.5.9");var subQ189=sQuery(id+"F0.wireOp",EDGE,"E3.0.5.10");var subQ190=sQuery(id+"F0.wireOp",EDGE,"E3.0.5.11");var subQ191=sQuery(id+"F0.wireOp",EDGE,"E3.0.5.12");var subQ192=sQuery(id+"F0.wireOp",EDGE,"E3.0.5.13");var subQ193=sQuery(id+"F0.wireOp",EDGE,"E3.0.5.14");var subQ194=sQuery(id+"F0.wireOp",EDGE,"E3.0.6.0");var subQ195=sQuery(id+"F0.wireOp",EDGE,"E3.0.6.1");var subQ196=sQuery(id+"F0.wireOp",EDGE,"E3.0.6.2");var subQ197=sQuery(id+"F0.wireOp",EDGE,"E3.0.6.3");var subQ198=sQuery(id+"F0.wireOp",EDGE,"E3.0.13.2");var subQ199=sQuery(id+"F0.wireOp",EDGE,"E3.0.13.3");var subQ200=sQuery(id+"F0.wireOp",EDGE,"E3.0.13.4");var subQ201=sQuery(id+"F0.wireOp",EDGE,"E3.0.13.5");var subQ202=sQuery(id+"F0.wireOp",EDGE,"E3.0.13.6");var subQ203=sQuery(id+"F0.wireOp",EDGE,"E3.0.13.7");var subQ204=sQuery(id+"F0.wireOp",EDGE,"E3.0.13.8");var subQ205=sQuery(id+"F0.wireOp",EDGE,"E3.0.13.9");var subQ206=sQuery(id+"F0.wireOp",EDGE,"E3.0.13.10");var subQ207=sQuery(id+"F0.wireOp",EDGE,"E3.0.13.11");var subQ208=sQuery(id+"F0.wireOp",EDGE,"E3.0.13.12");var subQ209=sQuery(id+"F0.wireOp",EDGE,"E3.0.13.13");var subQ210=sQuery(id+"F0.wireOp",EDGE,"E3.0.13.14");var subQ211=sQuery(id+"F0.wireOp",EDGE,"E3.0.14.0");var subQ212=sQuery(id+"F0.wireOp",EDGE,"E3.0.14.1");var subQ213=sQuery(id+"F0.wireOp",EDGE,"E3.0.14.2");var subQ214=sQuery(id+"F0.wireOp",EDGE,"E3.0.14.3");var subQ215=sQuery(id+"F0.wireOp",EDGE,"E3.0.14.4");var subQ216=sQuery(id+"F0.wireOp",EDGE,"E3.0.14.5");var subQ217=sQuery(id+"F0.wireOp",EDGE,"E3.0.14.6");var subQ218=sQuery(id+"F0.wireOp",EDGE,"E3.0.14.7");var subQ219=sQuery(id+"F0.wireOp",EDGE,"E3.0.14.8");var subQ220=sQuery(id+"F0.wireOp",EDGE,"E3.0.14.9");var subQ221=sQuery(id+"F0.wireOp",EDGE,"E3.0.14.10");var subQ222=sQuery(id+"F0.wireOp",EDGE,"E3.0.14.11");var subQ223=sQuery(id+"F0.wireOp",EDGE,"E3.0.14.12");var subQ224=sQuery(id+"F0.wireOp",EDGE,"E3.0.14.13");var subQ225=sQuery(id+"F0.wireOp",EDGE,"E3.0.14.14");Q0=makeQuery(id+"FJqtpdUANZnq3Um_1.boolean.opBoolean","SPLIT",FACE,{"disambiguationData":[TD([makeQuery(id+"F1.opExtrude","SWEPT_FACE",FACE,{"disambiguationData":[OSD([subQ144])]})])],"derivedFrom":makeQuery(id+"F1.opExtrude","CAP_FACE",FACE,{"disambiguationData":[OSD([sQuery(id+"F0.wireOp",EDGE,"E0.bottom"),subQ132,sQuery(id+"F0.wireOp",EDGE,"E0.left"),subQ135,subQ136,subQ137,subQ129,subQ128,subQ127,subQ126,subQ125,subQ124,subQ138,subQ139,subQ140,subQ141,subQ142,subQ143,sQuery(id+"F0.wireOp",EDGE,"E2.0.14.0"),subQ144,subQ145,subQ146,subQ147,subQ148,subQ134,subQ123,subQ122,subQ121,subQ120,subQ119,subQ118,subQ117,subQ116,subQ115,subQ114,subQ113,subQ112,subQ111,subQ110,subQ109,subQ108,subQ107,subQ106,subQ105,subQ104,subQ103,subQ102,subQ101,subQ130,subQ149,subQ150,subQ151,subQ152,subQ153,subQ154,subQ155,subQ156,subQ157,subQ158,subQ159,subQ160,subQ161,subQ162,subQ163,subQ164,subQ165,subQ166,subQ167,subQ168,subQ169,subQ170,subQ171,subQ172,subQ173,subQ174,subQ175,subQ176,subQ177,subQ178,subQ179,subQ180,subQ181,subQ182,subQ183,subQ184,subQ185,subQ186,subQ187,subQ188,subQ189,subQ190,subQ191,subQ192,subQ193,subQ194,subQ195,subQ196,subQ197,subQ133,subQ100,subQ99,subQ98,subQ97,subQ96,subQ95,subQ94,subQ93,subQ92,subQ91,subQ90,subQ89,subQ88,subQ87,subQ86,subQ85,subQ84,subQ83,subQ82,subQ81,subQ80,subQ79,subQ78,subQ77,subQ76,subQ75,subQ74,subQ73,subQ72,subQ71,subQ70,subQ69,subQ68,subQ67,subQ66,subQ65,subQ64,subQ63,subQ62,subQ61,subQ60,subQ59,subQ58,subQ57,subQ56,subQ55,subQ54,subQ53,subQ52,subQ51,subQ50,subQ49,subQ48,subQ47,subQ46,subQ45,subQ44,subQ43,subQ42,subQ41,subQ40,subQ39,subQ38,subQ37,subQ36,subQ35,subQ34,subQ33,subQ32,subQ31,subQ30,subQ29,subQ28,subQ27,subQ26,subQ25,subQ24,subQ23,subQ22,subQ21,subQ20,subQ19,subQ18,subQ17,subQ16,subQ15,subQ14,subQ13,subQ12,subQ11,subQ10,subQ9,subQ8,subQ7,subQ6,subQ5,subQ4,subQ3,subQ2,subQ1,subQ0,subQ131,subQ198,subQ199,subQ200,subQ201,subQ202,subQ203,subQ204,subQ205,subQ206,subQ207,subQ208,subQ209,subQ210,subQ211,subQ212,subQ213,subQ214,subQ215,subQ216,subQ217,subQ218,subQ219,subQ220,subQ221,subQ222,subQ223,subQ224,subQ225])],"isStart":false})});}
            var sketch = newSketch(context, id + "F7", { "sketchPlane" : qUnion([Q0])});
            skCircle(sketch, "E22", {"center": v(-162, 18) * mm, "radius": 2 * mm});
            skCircle(sketch, "E23.0.1.0", {"center": v(-162, 6) * mm, "radius": 2 * mm});
            skCircle(sketch, "E23.0.2.0", {"center": v(-162, -6) * mm, "radius": 2 * mm});
            skCircle(sketch, "E23.0.3.0", {"center": v(-162, -18) * mm, "radius": 2 * mm});
            skCircle(sketch, "E23.0.4.0", {"center": v(-162, -30) * mm, "radius": 2 * mm});
            skCircle(sketch, "E23.0.5.0", {"center": v(-162, -42) * mm, "radius": 2 * mm});
            skCircle(sketch, "E23.0.6.0", {"center": v(-162, -54) * mm, "radius": 2 * mm});
            skCircle(sketch, "E23.0.7.0", {"center": v(-162, -66) * mm, "radius": 2 * mm});
            skCircle(sketch, "E23.0.8.0", {"center": v(-162, -78) * mm, "radius": 2 * mm});
            skCircle(sketch, "E23.0.9.0", {"center": v(-162, -90) * mm, "radius": 2 * mm});
            skCircle(sketch, "E23.0.10.0", {"center": v(-162, -102) * mm, "radius": 2 * mm});
            skCircle(sketch, "E23.1.0.0", {"center": v(-150, 18) * mm, "radius": 2 * mm});
            skCircle(sketch, "E23.1.1.0", {"center": v(-150, 6) * mm, "radius": 2 * mm});
            skCircle(sketch, "E23.1.2.0", {"center": v(-150, -6) * mm, "radius": 2 * mm});
            skCircle(sketch, "E23.1.3.0", {"center": v(-150, -18) * mm, "radius": 2 * mm});
            skCircle(sketch, "E23.1.4.0", {"center": v(-150, -30) * mm, "radius": 2 * mm});
            skCircle(sketch, "E23.1.5.0", {"center": v(-150, -42) * mm, "radius": 2 * mm});
            skCircle(sketch, "E23.1.6.0", {"center": v(-150, -54) * mm, "radius": 2 * mm});
            skCircle(sketch, "E23.1.7.0", {"center": v(-150, -66) * mm, "radius": 2 * mm});
            skCircle(sketch, "E23.1.8.0", {"center": v(-150, -78) * mm, "radius": 2 * mm});
            skCircle(sketch, "E23.1.9.0", {"center": v(-150, -90) * mm, "radius": 2 * mm});
            skCircle(sketch, "E23.1.10.0", {"center": v(-150, -102) * mm, "radius": 2 * mm});
            skCircle(sketch, "E23.2.0.0", {"center": v(-138, 18) * mm, "radius": 2 * mm});
            skCircle(sketch, "E23.2.1.0", {"center": v(-138, 6) * mm, "radius": 2 * mm});
            skCircle(sketch, "E23.2.2.0", {"center": v(-138, -6) * mm, "radius": 2 * mm});
            skCircle(sketch, "E23.2.3.0", {"center": v(-138, -18) * mm, "radius": 2 * mm});
            skCircle(sketch, "E23.2.4.0", {"center": v(-138, -30) * mm, "radius": 2 * mm});
            skCircle(sketch, "E23.2.5.0", {"center": v(-138, -42) * mm, "radius": 2 * mm});
            skCircle(sketch, "E23.2.6.0", {"center": v(-138, -54) * mm, "radius": 2 * mm});
            skCircle(sketch, "E23.2.7.0", {"center": v(-138, -66) * mm, "radius": 2 * mm});
            skCircle(sketch, "E23.2.8.0", {"center": v(-138, -78) * mm, "radius": 2 * mm});
            skCircle(sketch, "E23.2.9.0", {"center": v(-138, -90) * mm, "radius": 2 * mm});
            skCircle(sketch, "E23.2.10.0", {"center": v(-138, -102) * mm, "radius": 2 * mm});
            skCircle(sketch, "E23.3.0.0", {"center": v(-126, 18) * mm, "radius": 2 * mm});
            skCircle(sketch, "E23.3.1.0", {"center": v(-126, 6) * mm, "radius": 2 * mm});
            skCircle(sketch, "E23.3.2.0", {"center": v(-126, -6) * mm, "radius": 2 * mm});
            skCircle(sketch, "E23.3.3.0", {"center": v(-126, -18) * mm, "radius": 2 * mm});
            skCircle(sketch, "E23.3.4.0", {"center": v(-126, -30) * mm, "radius": 2 * mm});
            skCircle(sketch, "E23.3.5.0", {"center": v(-126, -42) * mm, "radius": 2 * mm});
            skCircle(sketch, "E23.3.6.0", {"center": v(-126, -54) * mm, "radius": 2 * mm});
            skCircle(sketch, "E23.3.7.0", {"center": v(-126, -66) * mm, "radius": 2 * mm});
            skCircle(sketch, "E23.3.8.0", {"center": v(-126, -78) * mm, "radius": 2 * mm});
            skCircle(sketch, "E23.3.9.0", {"center": v(-126, -90) * mm, "radius": 2 * mm});
            skCircle(sketch, "E23.3.10.0", {"center": v(-126, -102) * mm, "radius": 2 * mm});
            skCircle(sketch, "E23.4.0.0", {"center": v(-114, 18) * mm, "radius": 2 * mm});
            skCircle(sketch, "E23.4.1.0", {"center": v(-114, 6) * mm, "radius": 2 * mm});
            skCircle(sketch, "E23.4.2.0", {"center": v(-114, -6) * mm, "radius": 2 * mm});
            skCircle(sketch, "E23.4.3.0", {"center": v(-114, -18) * mm, "radius": 2 * mm});
            skCircle(sketch, "E23.4.4.0", {"center": v(-114, -30) * mm, "radius": 2 * mm});
            skCircle(sketch, "E23.4.5.0", {"center": v(-114, -42) * mm, "radius": 2 * mm});
            skCircle(sketch, "E23.4.6.0", {"center": v(-114, -54) * mm, "radius": 2 * mm});
            skCircle(sketch, "E23.4.7.0", {"center": v(-114, -66) * mm, "radius": 2 * mm});
            skCircle(sketch, "E23.4.8.0", {"center": v(-114, -78) * mm, "radius": 2 * mm});
            skCircle(sketch, "E23.4.9.0", {"center": v(-114, -90) * mm, "radius": 2 * mm});
            skCircle(sketch, "E23.4.10.0", {"center": v(-114, -102) * mm, "radius": 2 * mm});
            skCircle(sketch, "E23.5.0.0", {"center": v(-102, 18) * mm, "radius": 2 * mm});
            skCircle(sketch, "E23.5.1.0", {"center": v(-102, 6) * mm, "radius": 2 * mm});
            skCircle(sketch, "E23.5.2.0", {"center": v(-102, -6) * mm, "radius": 2 * mm});
            skCircle(sketch, "E23.5.3.0", {"center": v(-102, -18) * mm, "radius": 2 * mm});
            skCircle(sketch, "E23.5.4.0", {"center": v(-102, -30) * mm, "radius": 2 * mm});
            skCircle(sketch, "E23.5.5.0", {"center": v(-102, -42) * mm, "radius": 2 * mm});
            skCircle(sketch, "E23.5.6.0", {"center": v(-102, -54) * mm, "radius": 2 * mm});
            skCircle(sketch, "E23.5.7.0", {"center": v(-102, -66) * mm, "radius": 2 * mm});
            skCircle(sketch, "E23.5.8.0", {"center": v(-102, -78) * mm, "radius": 2 * mm});
            skCircle(sketch, "E23.5.9.0", {"center": v(-102, -90) * mm, "radius": 2 * mm});
            skCircle(sketch, "E23.5.10.0", {"center": v(-102, -102) * mm, "radius": 2 * mm});
            skCircle(sketch, "E23.6.0.0", {"center": v(-90, 18) * mm, "radius": 2 * mm});
            skCircle(sketch, "E23.6.1.0", {"center": v(-90, 6) * mm, "radius": 2 * mm});
            skCircle(sketch, "E23.6.2.0", {"center": v(-90, -6) * mm, "radius": 2 * mm});
            skCircle(sketch, "E23.6.3.0", {"center": v(-90, -18) * mm, "radius": 2 * mm});
            skCircle(sketch, "E23.6.4.0", {"center": v(-90, -30) * mm, "radius": 2 * mm});
            skCircle(sketch, "E23.6.5.0", {"center": v(-90, -42) * mm, "radius": 2 * mm});
            skCircle(sketch, "E23.6.6.0", {"center": v(-90, -54) * mm, "radius": 2 * mm});
            skCircle(sketch, "E23.6.7.0", {"center": v(-90, -66) * mm, "radius": 2 * mm});
            skCircle(sketch, "E23.6.8.0", {"center": v(-90, -78) * mm, "radius": 2 * mm});
            skCircle(sketch, "E23.6.9.0", {"center": v(-90, -90) * mm, "radius": 2 * mm});
            skCircle(sketch, "E23.6.10.0", {"center": v(-90, -102) * mm, "radius": 2 * mm});
            skCircle(sketch, "E23.7.0.0", {"center": v(-78, 18) * mm, "radius": 2 * mm});
            skCircle(sketch, "E23.7.1.0", {"center": v(-78, 6) * mm, "radius": 2 * mm});
            skCircle(sketch, "E23.7.2.0", {"center": v(-78, -6) * mm, "radius": 2 * mm});
            skCircle(sketch, "E23.7.3.0", {"center": v(-78, -18) * mm, "radius": 2 * mm});
            skCircle(sketch, "E23.7.4.0", {"center": v(-78, -30) * mm, "radius": 2 * mm});
            skCircle(sketch, "E23.7.5.0", {"center": v(-78, -42) * mm, "radius": 2 * mm});
            skCircle(sketch, "E23.7.6.0", {"center": v(-78, -54) * mm, "radius": 2 * mm});
            skCircle(sketch, "E23.7.7.0", {"center": v(-78, -66) * mm, "radius": 2 * mm});
            skCircle(sketch, "E23.7.8.0", {"center": v(-78, -78) * mm, "radius": 2 * mm});
            skCircle(sketch, "E23.7.9.0", {"center": v(-78, -90) * mm, "radius": 2 * mm});
            skCircle(sketch, "E23.7.10.0", {"center": v(-78, -102) * mm, "radius": 2 * mm});
            skCircle(sketch, "E23.8.0.0", {"center": v(-66, 18) * mm, "radius": 2 * mm});
            skCircle(sketch, "E23.8.1.0", {"center": v(-66, 6) * mm, "radius": 2 * mm});
            skCircle(sketch, "E23.8.2.0", {"center": v(-66, -6) * mm, "radius": 2 * mm});
            skCircle(sketch, "E23.8.3.0", {"center": v(-66, -18) * mm, "radius": 2 * mm});
            skCircle(sketch, "E23.8.4.0", {"center": v(-66, -30) * mm, "radius": 2 * mm});
            skCircle(sketch, "E23.8.5.0", {"center": v(-66, -42) * mm, "radius": 2 * mm});
            skCircle(sketch, "E23.8.6.0", {"center": v(-66, -54) * mm, "radius": 2 * mm});
            skCircle(sketch, "E23.8.7.0", {"center": v(-66, -66) * mm, "radius": 2 * mm});
            skCircle(sketch, "E23.8.8.0", {"center": v(-66, -78) * mm, "radius": 2 * mm});
            skCircle(sketch, "E23.8.9.0", {"center": v(-66, -90) * mm, "radius": 2 * mm});
            skCircle(sketch, "E23.8.10.0", {"center": v(-66, -102) * mm, "radius": 2 * mm});
            skCircle(sketch, "E23.9.0.0", {"center": v(-54, 18) * mm, "radius": 2 * mm});
            skCircle(sketch, "E23.9.1.0", {"center": v(-54, 6) * mm, "radius": 2 * mm});
            skCircle(sketch, "E23.9.2.0", {"center": v(-54, -6) * mm, "radius": 2 * mm});
            skCircle(sketch, "E23.9.3.0", {"center": v(-54, -18) * mm, "radius": 2 * mm});
            skCircle(sketch, "E23.9.4.0", {"center": v(-54, -30) * mm, "radius": 2 * mm});
            skCircle(sketch, "E23.9.5.0", {"center": v(-54, -42) * mm, "radius": 2 * mm});
            skCircle(sketch, "E23.9.6.0", {"center": v(-54, -54) * mm, "radius": 2 * mm});
            skCircle(sketch, "E23.9.7.0", {"center": v(-54, -66) * mm, "radius": 2 * mm});
            skCircle(sketch, "E23.9.8.0", {"center": v(-54, -78) * mm, "radius": 2 * mm});
            skCircle(sketch, "E23.9.9.0", {"center": v(-54, -90) * mm, "radius": 2 * mm});
            skCircle(sketch, "E23.9.10.0", {"center": v(-54, -102) * mm, "radius": 2 * mm});
            skCircle(sketch, "E23.10.0.0", {"center": v(-42, 18) * mm, "radius": 2 * mm});
            skCircle(sketch, "E23.10.1.0", {"center": v(-42, 6) * mm, "radius": 2 * mm});
            skCircle(sketch, "E23.10.2.0", {"center": v(-42, -6) * mm, "radius": 2 * mm});
            skCircle(sketch, "E23.10.3.0", {"center": v(-42, -18) * mm, "radius": 2 * mm});
            skCircle(sketch, "E23.10.4.0", {"center": v(-42, -30) * mm, "radius": 2 * mm});
            skCircle(sketch, "E23.10.5.0", {"center": v(-42, -42) * mm, "radius": 2 * mm});
            skCircle(sketch, "E23.10.6.0", {"center": v(-42, -54) * mm, "radius": 2 * mm});
            skCircle(sketch, "E23.10.7.0", {"center": v(-42, -66) * mm, "radius": 2 * mm});
            skCircle(sketch, "E23.10.8.0", {"center": v(-42, -78) * mm, "radius": 2 * mm});
            skCircle(sketch, "E23.10.9.0", {"center": v(-42, -90) * mm, "radius": 2 * mm});
            skCircle(sketch, "E23.10.10.0", {"center": v(-42, -102) * mm, "radius": 2 * mm});
            skLineSegment(sketch, "E23.direction1", {"start": v(-162, 18) * mm, "end": v(-150, 18) * mm, "construction": true});
            skLineSegment(sketch, "E23.direction2", {"start": v(-162, 18) * mm, "end": v(-162, 6) * mm, "construction": true});
            skSolve(sketch);
        }
        {
            var Q0;
            Q0=qSketchRegion(id+"F7",true);
            extrude(context, id + "F8", {"entities" : qUnion([Q0]), "operationType" : NewBodyOperationType.REMOVE, "oppositeDirection" : true, "depth" : 1.5 * mm});
        }
        {
            var Q0;
            Q0=qSketchRegion(id+"F2",true);
            extrude(context, id + "F9", {"entities" : qUnion([Q0]), "operationType" : NewBodyOperationType.REMOVE, "oppositeDirection" : true, "depth" : 1 * mm});
        }
        {
            var Q0;
            Q0=qSketchRegion(id+"F3",true);
            extrude(context, id + "F10", {"entities" : qUnion([Q0]), "operationType" : NewBodyOperationType.REMOVE, "oppositeDirection" : true, "depth" : 1 * mm});
        }
        {
            var Q0;
            Q0=qSketchRegion(id+"F4",true);
            extrude(context, id + "F11", {"entities" : qUnion([Q0]), "operationType" : NewBodyOperationType.REMOVE, "oppositeDirection" : true, "depth" : 1 * mm});
        }
    });
